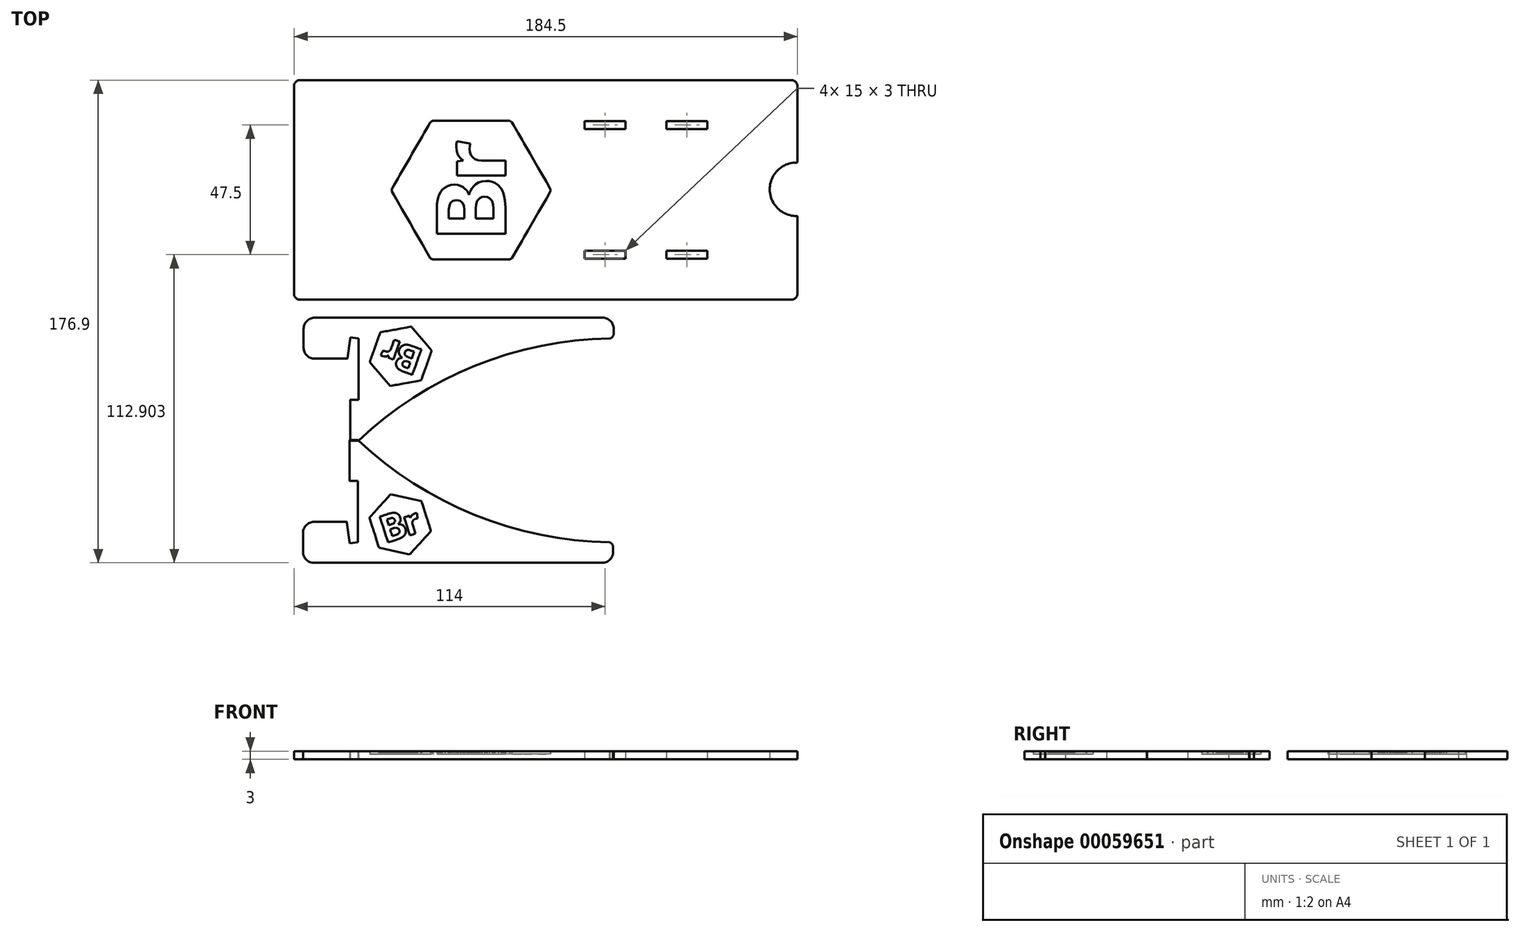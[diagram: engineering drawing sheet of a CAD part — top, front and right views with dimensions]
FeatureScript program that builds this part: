
annotation { "Feature Type Name" : "Feature", "Feature Type Description" : "" }
export const myFeature = defineFeature(function(context is Context, id is Id, definition is map)
    precondition{}
    {
        {
            var Q0;
            Q0=qCreatedBy(makeId("Top.planeOp"),FACE);
            var sketch = newSketch(context, id + "F0", { "sketchPlane" : qUnion([Q0])});
            skLineSegment(sketch, "E0", {"start": v(-68.83, -88.45) * mm, "end": v(20.7, -88.45) * mm});
            skArc(sketch, "E1", {"start": v(20.7, -88.45) * mm, "mid": v(23.52, -87.28) * mm, "end": v(24.7, -84.45) * mm});
            skLineSegment(sketch, "E2", {"start": v(24.7, -84.45) * mm, "end": v(24.7, -82.65) * mm});
            skArc(sketch, "E3", {"start": v(24.7, -82.65) * mm, "mid": v(24.69, -82.75) * mm, "end": v(24.68, -82.85) * mm});
            skLineSegment(sketch, "E4", {"start": v(24.68, -82.85) * mm, "end": v(24.7, -82.63) * mm});
            skArc(sketch, "E5", {"start": v(24.7, -82.63) * mm, "mid": v(24.29, -81.5) * mm, "end": v(23.26, -80.88) * mm});
            skArc(sketch, "E6", {"start": v(23.26, -80.88) * mm, "mid": v(-26.29, -70.78) * mm, "end": v(-68.83, -43.45) * mm});
            skLineSegment(sketch, "E7", {"start": v(-68.83, -43.45) * mm, "end": v(-71.63, -43.45) * mm});
            skArc(sketch, "E8", {"start": v(-71.63, -43.45) * mm, "mid": v(-71.77, -43.51) * mm, "end": v(-71.83, -43.65) * mm});
            skLineSegment(sketch, "E9", {"start": v(-71.83, -43.65) * mm, "end": v(-71.83, -58.25) * mm});
            skArc(sketch, "E10", {"start": v(-71.83, -58.25) * mm, "mid": v(-71.77, -58.4) * mm, "end": v(-71.63, -58.45) * mm});
            skLineSegment(sketch, "E11", {"start": v(-71.63, -58.45) * mm, "end": v(-68.83, -58.45) * mm});
            skLineSegment(sketch, "E12", {"start": v(-68.83, -58.45) * mm, "end": v(-68.83, -73.45) * mm});
            skLineSegment(sketch, "E13", {"start": v(-68.83, -73.45) * mm, "end": v(-68.83, -80.9) * mm});
            skLineSegment(sketch, "E14", {"start": v(-68.83, -80.9) * mm, "end": v(-71.8, -81.3) * mm});
            skLineSegment(sketch, "E15", {"start": v(-71.8, -81.3) * mm, "end": v(-71.86, -80.9) * mm});
            skLineSegment(sketch, "E16", {"start": v(-71.86, -80.9) * mm, "end": v(-72.83, -73.63) * mm});
            skArc(sketch, "E17", {"start": v(-72.83, -73.63) * mm, "mid": v(-72.9, -73.5) * mm, "end": v(-73.03, -73.45) * mm});
            skLineSegment(sketch, "E18", {"start": v(-73.03, -73.45) * mm, "end": v(-84.9, -73.45) * mm});
            skArc(sketch, "E19", {"start": v(-84.9, -73.45) * mm, "mid": v(-87.74, -74.62) * mm, "end": v(-88.9, -77.45) * mm});
            skLineSegment(sketch, "E20", {"start": v(-88.9, -77.45) * mm, "end": v(-88.9, -84.45) * mm});
            skArc(sketch, "E21", {"start": v(-88.9, -84.45) * mm, "mid": v(-87.74, -87.28) * mm, "end": v(-84.9, -88.45) * mm});
            skLineSegment(sketch, "E22", {"start": v(-84.9, -88.45) * mm, "end": v(-71.83, -88.45) * mm});
            skLineSegment(sketch, "E23", {"start": v(-71.83, -88.45) * mm, "end": v(-68.83, -88.45) * mm});
            skLineSegment(sketch, "E24", {"start": v(-68.83, -88.45) * mm, "end": v(-68.83, -88.45) * mm});
            skLineSegment(sketch, "E25", {"start": v(-68.63, 1.35) * mm, "end": v(20.9, 1.35) * mm});
            skArc(sketch, "E26", {"start": v(20.9, 1.35) * mm, "mid": v(23.72, 0.18) * mm, "end": v(24.9, -2.65) * mm});
            skLineSegment(sketch, "E27", {"start": v(24.9, -2.65) * mm, "end": v(24.9, -4.45) * mm});
            skArc(sketch, "E28", {"start": v(24.9, -4.45) * mm, "mid": v(24.89, -4.36) * mm, "end": v(24.88, -4.26) * mm});
            skLineSegment(sketch, "E29", {"start": v(24.88, -4.26) * mm, "end": v(24.9, -4.47) * mm});
            skArc(sketch, "E30", {"start": v(24.9, -4.47) * mm, "mid": v(24.49, -5.6) * mm, "end": v(23.46, -6.22) * mm});
            skArc(sketch, "E31", {"start": v(23.46, -6.22) * mm, "mid": v(-26.09, -16.32) * mm, "end": v(-68.63, -43.65) * mm});
            skLineSegment(sketch, "E32", {"start": v(-68.63, -43.65) * mm, "end": v(-71.43, -43.65) * mm});
            skArc(sketch, "E33", {"start": v(-71.43, -43.65) * mm, "mid": v(-71.57, -43.6) * mm, "end": v(-71.63, -43.45) * mm});
            skLineSegment(sketch, "E34", {"start": v(-71.63, -43.45) * mm, "end": v(-71.63, -28.85) * mm});
            skArc(sketch, "E35", {"start": v(-71.63, -28.85) * mm, "mid": v(-71.57, -28.71) * mm, "end": v(-71.43, -28.65) * mm});
            skLineSegment(sketch, "E36", {"start": v(-71.43, -28.65) * mm, "end": v(-68.63, -28.65) * mm});
            skLineSegment(sketch, "E37", {"start": v(-68.63, -28.65) * mm, "end": v(-68.63, -13.65) * mm});
            skLineSegment(sketch, "E38", {"start": v(-68.63, -13.65) * mm, "end": v(-68.63, -6.2) * mm});
            skLineSegment(sketch, "E39", {"start": v(-68.63, -6.2) * mm, "end": v(-71.6, -5.8) * mm});
            skLineSegment(sketch, "E40", {"start": v(-71.6, -5.8) * mm, "end": v(-71.66, -6.2) * mm});
            skLineSegment(sketch, "E41", {"start": v(-71.66, -6.2) * mm, "end": v(-72.63, -13.48) * mm});
            skArc(sketch, "E42", {"start": v(-72.63, -13.48) * mm, "mid": v(-72.7, -13.6) * mm, "end": v(-72.83, -13.65) * mm});
            skLineSegment(sketch, "E43", {"start": v(-72.83, -13.65) * mm, "end": v(-84.7, -13.65) * mm});
            skArc(sketch, "E44", {"start": v(-84.7, -13.65) * mm, "mid": v(-87.54, -12.48) * mm, "end": v(-88.7, -9.65) * mm});
            skLineSegment(sketch, "E45", {"start": v(-88.7, -9.65) * mm, "end": v(-88.7, -2.65) * mm});
            skArc(sketch, "E46", {"start": v(-88.7, -2.65) * mm, "mid": v(-87.54, 0.18) * mm, "end": v(-84.7, 1.35) * mm});
            skLineSegment(sketch, "E47", {"start": v(-84.7, 1.35) * mm, "end": v(-71.63, 1.35) * mm});
            skLineSegment(sketch, "E48", {"start": v(-71.63, 1.35) * mm, "end": v(-68.63, 1.35) * mm});
            skLineSegment(sketch, "E49", {"start": v(-68.63, 1.35) * mm, "end": v(-68.63, 1.35) * mm});
            skLineSegment(sketch, "E50", {"start": v(92, 58.23) * mm, "end": v(92, 58.23) * mm});
            skLineSegment(sketch, "E51", {"start": v(92, 58.23) * mm, "end": v(91.87, 58.23) * mm});
            skArc(sketch, "E52", {"start": v(91.87, 58.23) * mm, "mid": v(83.37, 53.32) * mm, "end": v(83.37, 43.52) * mm});
            skArc(sketch, "E53", {"start": v(83.37, 43.52) * mm, "mid": v(87.02, 39.9) * mm, "end": v(92, 38.61) * mm});
            skArc(sketch, "E54", {"start": v(92, 38.61) * mm, "mid": v(92.18, 38.54) * mm, "end": v(92.25, 38.36) * mm});
            skLineSegment(sketch, "E55", {"start": v(92.25, 38.36) * mm, "end": v(92.25, 10.2) * mm});
            skArc(sketch, "E56", {"start": v(92.25, 10.2) * mm, "mid": v(91.6, 8.61) * mm, "end": v(90, 7.95) * mm});
            skLineSegment(sketch, "E57", {"start": v(90, 7.95) * mm, "end": v(-28, 7.95) * mm});
            skLineSegment(sketch, "E58", {"start": v(-28, 7.95) * mm, "end": v(-90, 7.95) * mm});
            skArc(sketch, "E59", {"start": v(-90, 7.95) * mm, "mid": v(-91.6, 8.61) * mm, "end": v(-92.25, 10.2) * mm});
            skLineSegment(sketch, "E60", {"start": v(-92.25, 10.2) * mm, "end": v(-92.25, 86.2) * mm});
            skArc(sketch, "E61", {"start": v(-92.25, 86.2) * mm, "mid": v(-91.6, 87.8) * mm, "end": v(-90, 88.45) * mm});
            skLineSegment(sketch, "E62", {"start": v(-90, 88.45) * mm, "end": v(-28, 88.45) * mm});
            skLineSegment(sketch, "E63", {"start": v(-28, 88.45) * mm, "end": v(90, 88.45) * mm});
            skArc(sketch, "E64", {"start": v(90, 88.45) * mm, "mid": v(91.6, 87.8) * mm, "end": v(92.25, 86.2) * mm});
            skLineSegment(sketch, "E65", {"start": v(92.25, 86.2) * mm, "end": v(92.25, 86.05) * mm});
            skLineSegment(sketch, "E66", {"start": v(92.25, 86.05) * mm, "end": v(92.25, 58.48) * mm});
            skArc(sketch, "E67", {"start": v(92.25, 58.48) * mm, "mid": v(92.18, 58.3) * mm, "end": v(92, 58.23) * mm});
            skLineSegment(sketch, "E68", {"start": v(-42.29, 72.97) * mm, "end": v(-43.03, 71.69) * mm});
            skLineSegment(sketch, "E69", {"start": v(-43.03, 71.69) * mm, "end": v(-43.77, 70.4) * mm});
            skLineSegment(sketch, "E70", {"start": v(-43.77, 70.4) * mm, "end": v(-44.5, 69.12) * mm});
            skLineSegment(sketch, "E71", {"start": v(-44.5, 69.12) * mm, "end": v(-45.25, 67.83) * mm});
            skLineSegment(sketch, "E72", {"start": v(-45.25, 67.83) * mm, "end": v(-46, 66.55) * mm});
            skLineSegment(sketch, "E73", {"start": v(-46, 66.55) * mm, "end": v(-46.73, 65.26) * mm});
            skLineSegment(sketch, "E74", {"start": v(-46.73, 65.26) * mm, "end": v(-47.48, 63.98) * mm});
            skLineSegment(sketch, "E75", {"start": v(-47.48, 63.98) * mm, "end": v(-48.22, 62.7) * mm});
            skLineSegment(sketch, "E76", {"start": v(-48.22, 62.7) * mm, "end": v(-48.96, 61.41) * mm});
            skLineSegment(sketch, "E77", {"start": v(-48.96, 61.41) * mm, "end": v(-49.7, 60.13) * mm});
            skLineSegment(sketch, "E78", {"start": v(-49.7, 60.13) * mm, "end": v(-50.44, 58.84) * mm});
            skLineSegment(sketch, "E79", {"start": v(-50.44, 58.84) * mm, "end": v(-51.18, 57.56) * mm});
            skLineSegment(sketch, "E80", {"start": v(-51.18, 57.56) * mm, "end": v(-51.92, 56.27) * mm});
            skLineSegment(sketch, "E81", {"start": v(-51.92, 56.27) * mm, "end": v(-52.67, 55) * mm});
            skLineSegment(sketch, "E82", {"start": v(-52.67, 55) * mm, "end": v(-53.4, 53.7) * mm});
            skLineSegment(sketch, "E83", {"start": v(-53.4, 53.7) * mm, "end": v(-54.15, 52.42) * mm});
            skLineSegment(sketch, "E84", {"start": v(-54.15, 52.42) * mm, "end": v(-54.9, 51.14) * mm});
            skLineSegment(sketch, "E85", {"start": v(-54.9, 51.14) * mm, "end": v(-55.63, 49.85) * mm});
            skLineSegment(sketch, "E86", {"start": v(-55.63, 49.85) * mm, "end": v(-56.37, 48.57) * mm});
            skLineSegment(sketch, "E87", {"start": v(-56.37, 48.57) * mm, "end": v(-56.37, 47.58) * mm});
            skLineSegment(sketch, "E88", {"start": v(-56.37, 47.58) * mm, "end": v(-55.63, 46.3) * mm});
            skLineSegment(sketch, "E89", {"start": v(-55.63, 46.3) * mm, "end": v(-54.9, 45) * mm});
            skLineSegment(sketch, "E90", {"start": v(-54.9, 45) * mm, "end": v(-54.15, 43.72) * mm});
            skLineSegment(sketch, "E91", {"start": v(-54.15, 43.72) * mm, "end": v(-53.4, 42.44) * mm});
            skLineSegment(sketch, "E92", {"start": v(-53.4, 42.44) * mm, "end": v(-52.67, 41.15) * mm});
            skLineSegment(sketch, "E93", {"start": v(-52.67, 41.15) * mm, "end": v(-51.92, 39.87) * mm});
            skLineSegment(sketch, "E94", {"start": v(-51.92, 39.87) * mm, "end": v(-51.18, 38.59) * mm});
            skLineSegment(sketch, "E95", {"start": v(-51.18, 38.59) * mm, "end": v(-50.44, 37.3) * mm});
            skLineSegment(sketch, "E96", {"start": v(-50.44, 37.3) * mm, "end": v(-49.7, 36.02) * mm});
            skLineSegment(sketch, "E97", {"start": v(-49.7, 36.02) * mm, "end": v(-48.96, 34.73) * mm});
            skLineSegment(sketch, "E98", {"start": v(-48.96, 34.73) * mm, "end": v(-48.22, 33.45) * mm});
            skLineSegment(sketch, "E99", {"start": v(-48.22, 33.45) * mm, "end": v(-47.48, 32.16) * mm});
            skLineSegment(sketch, "E100", {"start": v(-47.48, 32.16) * mm, "end": v(-46.73, 30.88) * mm});
            skLineSegment(sketch, "E101", {"start": v(-46.73, 30.88) * mm, "end": v(-46, 29.6) * mm});
            skLineSegment(sketch, "E102", {"start": v(-46, 29.6) * mm, "end": v(-45.25, 28.3) * mm});
            skLineSegment(sketch, "E103", {"start": v(-45.25, 28.3) * mm, "end": v(-44.5, 27.02) * mm});
            skLineSegment(sketch, "E104", {"start": v(-44.5, 27.02) * mm, "end": v(-43.77, 25.74) * mm});
            skLineSegment(sketch, "E105", {"start": v(-43.77, 25.74) * mm, "end": v(-43.03, 24.45) * mm});
            skLineSegment(sketch, "E106", {"start": v(-43.03, 24.45) * mm, "end": v(-42.29, 23.17) * mm});
            skLineSegment(sketch, "E107", {"start": v(-42.29, 23.17) * mm, "end": v(-41.42, 22.67) * mm});
            skLineSegment(sketch, "E108", {"start": v(-41.42, 22.67) * mm, "end": v(-39.94, 22.67) * mm});
            skLineSegment(sketch, "E109", {"start": v(-39.94, 22.67) * mm, "end": v(-38.46, 22.67) * mm});
            skLineSegment(sketch, "E110", {"start": v(-38.46, 22.67) * mm, "end": v(-36.97, 22.67) * mm});
            skLineSegment(sketch, "E111", {"start": v(-36.97, 22.67) * mm, "end": v(-35.49, 22.67) * mm});
            skLineSegment(sketch, "E112", {"start": v(-35.49, 22.67) * mm, "end": v(-34, 22.67) * mm});
            skLineSegment(sketch, "E113", {"start": v(-34, 22.67) * mm, "end": v(-32.52, 22.67) * mm});
            skLineSegment(sketch, "E114", {"start": v(-32.52, 22.67) * mm, "end": v(-31.04, 22.67) * mm});
            skLineSegment(sketch, "E115", {"start": v(-31.04, 22.67) * mm, "end": v(-29.56, 22.67) * mm});
            skLineSegment(sketch, "E116", {"start": v(-29.56, 22.67) * mm, "end": v(-28.07, 22.67) * mm});
            skLineSegment(sketch, "E117", {"start": v(-28.07, 22.67) * mm, "end": v(-26.6, 22.67) * mm});
            skLineSegment(sketch, "E118", {"start": v(-26.6, 22.67) * mm, "end": v(-25.1, 22.67) * mm});
            skLineSegment(sketch, "E119", {"start": v(-25.1, 22.67) * mm, "end": v(-23.63, 22.67) * mm});
            skLineSegment(sketch, "E120", {"start": v(-23.63, 22.67) * mm, "end": v(-22.14, 22.67) * mm});
            skLineSegment(sketch, "E121", {"start": v(-22.14, 22.67) * mm, "end": v(-20.66, 22.67) * mm});
            skLineSegment(sketch, "E122", {"start": v(-20.66, 22.67) * mm, "end": v(-19.18, 22.67) * mm});
            skLineSegment(sketch, "E123", {"start": v(-19.18, 22.67) * mm, "end": v(-17.7, 22.67) * mm});
            skLineSegment(sketch, "E124", {"start": v(-17.7, 22.67) * mm, "end": v(-16.21, 22.67) * mm});
            skLineSegment(sketch, "E125", {"start": v(-16.21, 22.67) * mm, "end": v(-14.73, 22.67) * mm});
            skLineSegment(sketch, "E126", {"start": v(-14.73, 22.67) * mm, "end": v(-13.24, 22.67) * mm});
            skLineSegment(sketch, "E127", {"start": v(-13.24, 22.67) * mm, "end": v(-12.38, 23.17) * mm});
            skLineSegment(sketch, "E128", {"start": v(-12.38, 23.17) * mm, "end": v(-11.64, 24.45) * mm});
            skLineSegment(sketch, "E129", {"start": v(-11.64, 24.45) * mm, "end": v(-10.9, 25.74) * mm});
            skLineSegment(sketch, "E130", {"start": v(-10.9, 25.74) * mm, "end": v(-10.16, 27.02) * mm});
            skLineSegment(sketch, "E131", {"start": v(-10.16, 27.02) * mm, "end": v(-9.42, 28.3) * mm});
            skLineSegment(sketch, "E132", {"start": v(-9.42, 28.3) * mm, "end": v(-8.67, 29.6) * mm});
            skLineSegment(sketch, "E133", {"start": v(-8.67, 29.6) * mm, "end": v(-7.93, 30.87) * mm});
            skLineSegment(sketch, "E134", {"start": v(-7.93, 30.87) * mm, "end": v(-7.2, 32.16) * mm});
            skLineSegment(sketch, "E135", {"start": v(-7.2, 32.16) * mm, "end": v(-6.45, 33.44) * mm});
            skLineSegment(sketch, "E136", {"start": v(-6.45, 33.44) * mm, "end": v(-5.7, 34.73) * mm});
            skLineSegment(sketch, "E137", {"start": v(-5.7, 34.73) * mm, "end": v(-4.97, 36.01) * mm});
            skLineSegment(sketch, "E138", {"start": v(-4.97, 36.01) * mm, "end": v(-4.22, 37.3) * mm});
            skLineSegment(sketch, "E139", {"start": v(-4.22, 37.3) * mm, "end": v(-3.48, 38.58) * mm});
            skLineSegment(sketch, "E140", {"start": v(-3.48, 38.58) * mm, "end": v(-2.74, 39.86) * mm});
            skLineSegment(sketch, "E141", {"start": v(-2.74, 39.86) * mm, "end": v(-2, 41.15) * mm});
            skLineSegment(sketch, "E142", {"start": v(-2, 41.15) * mm, "end": v(-1.26, 42.43) * mm});
            skLineSegment(sketch, "E143", {"start": v(-1.26, 42.43) * mm, "end": v(-0.52, 43.72) * mm});
            skLineSegment(sketch, "E144", {"start": v(-0.52, 43.72) * mm, "end": v(0.22, 45) * mm});
            skLineSegment(sketch, "E145", {"start": v(0.22, 45) * mm, "end": v(0.97, 46.29) * mm});
            skLineSegment(sketch, "E146", {"start": v(0.97, 46.29) * mm, "end": v(1.7, 47.57) * mm});
            skLineSegment(sketch, "E147", {"start": v(1.7, 47.57) * mm, "end": v(1.84, 48.07) * mm});
            skLineSegment(sketch, "E148", {"start": v(1.84, 48.07) * mm, "end": v(1.7, 48.57) * mm});
            skLineSegment(sketch, "E149", {"start": v(1.7, 48.57) * mm, "end": v(0.97, 49.85) * mm});
            skLineSegment(sketch, "E150", {"start": v(0.97, 49.85) * mm, "end": v(0.22, 51.14) * mm});
            skLineSegment(sketch, "E151", {"start": v(0.22, 51.14) * mm, "end": v(-0.52, 52.42) * mm});
            skLineSegment(sketch, "E152", {"start": v(-0.52, 52.42) * mm, "end": v(-1.26, 53.7) * mm});
            skLineSegment(sketch, "E153", {"start": v(-1.26, 53.7) * mm, "end": v(-2, 55) * mm});
            skLineSegment(sketch, "E154", {"start": v(-2, 55) * mm, "end": v(-2.74, 56.28) * mm});
            skLineSegment(sketch, "E155", {"start": v(-2.74, 56.28) * mm, "end": v(-3.48, 57.56) * mm});
            skLineSegment(sketch, "E156", {"start": v(-3.48, 57.56) * mm, "end": v(-4.22, 58.85) * mm});
            skLineSegment(sketch, "E157", {"start": v(-4.22, 58.85) * mm, "end": v(-4.97, 60.13) * mm});
            skLineSegment(sketch, "E158", {"start": v(-4.97, 60.13) * mm, "end": v(-5.7, 61.42) * mm});
            skLineSegment(sketch, "E159", {"start": v(-5.7, 61.42) * mm, "end": v(-6.45, 62.7) * mm});
            skLineSegment(sketch, "E160", {"start": v(-6.45, 62.7) * mm, "end": v(-7.2, 63.99) * mm});
            skLineSegment(sketch, "E161", {"start": v(-7.2, 63.99) * mm, "end": v(-7.93, 65.27) * mm});
            skLineSegment(sketch, "E162", {"start": v(-7.93, 65.27) * mm, "end": v(-8.67, 66.55) * mm});
            skLineSegment(sketch, "E163", {"start": v(-8.67, 66.55) * mm, "end": v(-9.42, 67.84) * mm});
            skLineSegment(sketch, "E164", {"start": v(-9.42, 67.84) * mm, "end": v(-10.16, 69.12) * mm});
            skLineSegment(sketch, "E165", {"start": v(-10.16, 69.12) * mm, "end": v(-10.9, 70.4) * mm});
            skLineSegment(sketch, "E166", {"start": v(-10.9, 70.4) * mm, "end": v(-11.64, 71.7) * mm});
            skLineSegment(sketch, "E167", {"start": v(-11.64, 71.7) * mm, "end": v(-12.38, 72.98) * mm});
            skLineSegment(sketch, "E168", {"start": v(-12.38, 72.98) * mm, "end": v(-13.24, 73.48) * mm});
            skLineSegment(sketch, "E169", {"start": v(-13.24, 73.48) * mm, "end": v(-14.73, 73.48) * mm});
            skLineSegment(sketch, "E170", {"start": v(-14.73, 73.48) * mm, "end": v(-16.21, 73.48) * mm});
            skLineSegment(sketch, "E171", {"start": v(-16.21, 73.48) * mm, "end": v(-17.7, 73.48) * mm});
            skLineSegment(sketch, "E172", {"start": v(-17.7, 73.48) * mm, "end": v(-19.18, 73.48) * mm});
            skLineSegment(sketch, "E173", {"start": v(-19.18, 73.48) * mm, "end": v(-20.66, 73.48) * mm});
            skLineSegment(sketch, "E174", {"start": v(-20.66, 73.48) * mm, "end": v(-22.14, 73.48) * mm});
            skLineSegment(sketch, "E175", {"start": v(-22.14, 73.48) * mm, "end": v(-23.63, 73.48) * mm});
            skLineSegment(sketch, "E176", {"start": v(-23.63, 73.48) * mm, "end": v(-25.1, 73.48) * mm});
            skLineSegment(sketch, "E177", {"start": v(-25.1, 73.48) * mm, "end": v(-26.6, 73.48) * mm});
            skLineSegment(sketch, "E178", {"start": v(-26.6, 73.48) * mm, "end": v(-28.07, 73.48) * mm});
            skLineSegment(sketch, "E179", {"start": v(-28.07, 73.48) * mm, "end": v(-29.56, 73.48) * mm});
            skLineSegment(sketch, "E180", {"start": v(-29.56, 73.48) * mm, "end": v(-31.04, 73.48) * mm});
            skLineSegment(sketch, "E181", {"start": v(-31.04, 73.48) * mm, "end": v(-32.52, 73.48) * mm});
            skLineSegment(sketch, "E182", {"start": v(-32.52, 73.48) * mm, "end": v(-34, 73.48) * mm});
            skLineSegment(sketch, "E183", {"start": v(-34, 73.48) * mm, "end": v(-35.49, 73.48) * mm});
            skLineSegment(sketch, "E184", {"start": v(-35.49, 73.48) * mm, "end": v(-36.97, 73.48) * mm});
            skLineSegment(sketch, "E185", {"start": v(-36.97, 73.48) * mm, "end": v(-38.46, 73.48) * mm});
            skLineSegment(sketch, "E186", {"start": v(-38.46, 73.48) * mm, "end": v(-39.94, 73.48) * mm});
            skLineSegment(sketch, "E187", {"start": v(-39.94, 73.48) * mm, "end": v(-41.42, 73.48) * mm});
            skLineSegment(sketch, "E188", {"start": v(-41.42, 73.48) * mm, "end": v(-42.29, 72.97) * mm});
            skLineSegment(sketch, "E189", {"start": v(-29.84, 41.08) * mm, "end": v(-30, 42.34) * mm});
            skLineSegment(sketch, "E190", {"start": v(-30, 42.34) * mm, "end": v(-30.47, 43.43) * mm});
            skLineSegment(sketch, "E191", {"start": v(-30.47, 43.43) * mm, "end": v(-31.33, 44.2) * mm});
            skLineSegment(sketch, "E192", {"start": v(-31.33, 44.2) * mm, "end": v(-32.67, 44.5) * mm});
            skLineSegment(sketch, "E193", {"start": v(-32.67, 44.5) * mm, "end": v(-34.04, 44.2) * mm});
            skLineSegment(sketch, "E194", {"start": v(-34.04, 44.2) * mm, "end": v(-34.9, 43.41) * mm});
            skLineSegment(sketch, "E195", {"start": v(-34.9, 43.41) * mm, "end": v(-35.35, 42.3) * mm});
            skLineSegment(sketch, "E196", {"start": v(-35.35, 42.3) * mm, "end": v(-35.49, 41.08) * mm});
            skLineSegment(sketch, "E197", {"start": v(-35.49, 41.08) * mm, "end": v(-35.49, 39.96) * mm});
            skLineSegment(sketch, "E198", {"start": v(-35.49, 39.96) * mm, "end": v(-35.49, 38.84) * mm});
            skLineSegment(sketch, "E199", {"start": v(-35.49, 38.84) * mm, "end": v(-35.49, 37.72) * mm});
            skLineSegment(sketch, "E200", {"start": v(-35.49, 37.72) * mm, "end": v(-34.07, 37.72) * mm});
            skLineSegment(sketch, "E201", {"start": v(-34.07, 37.72) * mm, "end": v(-32.66, 37.72) * mm});
            skLineSegment(sketch, "E202", {"start": v(-32.66, 37.72) * mm, "end": v(-31.24, 37.72) * mm});
            skLineSegment(sketch, "E203", {"start": v(-31.24, 37.72) * mm, "end": v(-29.83, 37.72) * mm});
            skLineSegment(sketch, "E204", {"start": v(-29.83, 37.72) * mm, "end": v(-29.83, 38.84) * mm});
            skLineSegment(sketch, "E205", {"start": v(-29.83, 38.84) * mm, "end": v(-29.83, 39.96) * mm});
            skLineSegment(sketch, "E206", {"start": v(-29.83, 39.96) * mm, "end": v(-29.83, 41.08) * mm});
            skLineSegment(sketch, "E207", {"start": v(-29.83, 41.08) * mm, "end": v(-29.84, 41.08) * mm});
            skLineSegment(sketch, "E208", {"start": v(-32.44, 53.51) * mm, "end": v(-32.44, 54.81) * mm});
            skLineSegment(sketch, "E209", {"start": v(-32.44, 54.81) * mm, "end": v(-32.44, 56.11) * mm});
            skLineSegment(sketch, "E210", {"start": v(-32.44, 56.11) * mm, "end": v(-32.44, 57.41) * mm});
            skLineSegment(sketch, "E211", {"start": v(-32.44, 57.41) * mm, "end": v(-32.44, 58.71) * mm});
            skLineSegment(sketch, "E212", {"start": v(-32.44, 58.71) * mm, "end": v(-31.33, 58.8) * mm});
            skLineSegment(sketch, "E213", {"start": v(-31.33, 58.8) * mm, "end": v(-30.21, 58.9) * mm});
            skLineSegment(sketch, "E214", {"start": v(-30.21, 58.9) * mm, "end": v(-31.1, 59.7) * mm});
            skLineSegment(sketch, "E215", {"start": v(-31.1, 59.7) * mm, "end": v(-31.95, 60.76) * mm});
            skLineSegment(sketch, "E216", {"start": v(-31.95, 60.76) * mm, "end": v(-32.4, 61.63) * mm});
            skLineSegment(sketch, "E217", {"start": v(-32.4, 61.63) * mm, "end": v(-32.68, 62.65) * mm});
            skLineSegment(sketch, "E218", {"start": v(-32.68, 62.65) * mm, "end": v(-32.78, 63.83) * mm});
            skLineSegment(sketch, "E219", {"start": v(-32.78, 63.83) * mm, "end": v(-32.7, 65.06) * mm});
            skLineSegment(sketch, "E220", {"start": v(-32.7, 65.06) * mm, "end": v(-32.44, 66.06) * mm});
            skLineSegment(sketch, "E221", {"start": v(-32.44, 66.06) * mm, "end": v(-31.24, 65.84) * mm});
            skLineSegment(sketch, "E222", {"start": v(-31.24, 65.84) * mm, "end": v(-30.05, 65.63) * mm});
            skLineSegment(sketch, "E223", {"start": v(-30.05, 65.63) * mm, "end": v(-28.85, 65.41) * mm});
            skLineSegment(sketch, "E224", {"start": v(-28.85, 65.41) * mm, "end": v(-27.66, 65.2) * mm});
            skLineSegment(sketch, "E225", {"start": v(-27.66, 65.2) * mm, "end": v(-27.85, 64.3) * mm});
            skLineSegment(sketch, "E226", {"start": v(-27.85, 64.3) * mm, "end": v(-27.92, 63.24) * mm});
            skLineSegment(sketch, "E227", {"start": v(-27.92, 63.24) * mm, "end": v(-27.8, 62.04) * mm});
            skLineSegment(sketch, "E228", {"start": v(-27.8, 62.04) * mm, "end": v(-27.4, 61) * mm});
            skLineSegment(sketch, "E229", {"start": v(-27.4, 61) * mm, "end": v(-26.77, 60.13) * mm});
            skLineSegment(sketch, "E230", {"start": v(-26.77, 60.13) * mm, "end": v(-25.9, 59.48) * mm});
            skLineSegment(sketch, "E231", {"start": v(-25.9, 59.48) * mm, "end": v(-24.8, 59.08) * mm});
            skLineSegment(sketch, "E232", {"start": v(-24.8, 59.08) * mm, "end": v(-23.5, 58.95) * mm});
            skLineSegment(sketch, "E233", {"start": v(-23.5, 58.95) * mm, "end": v(-22.05, 58.95) * mm});
            skLineSegment(sketch, "E234", {"start": v(-22.05, 58.95) * mm, "end": v(-20.6, 58.95) * mm});
            skLineSegment(sketch, "E235", {"start": v(-20.6, 58.95) * mm, "end": v(-19.13, 58.95) * mm});
            skLineSegment(sketch, "E236", {"start": v(-19.13, 58.95) * mm, "end": v(-17.68, 58.95) * mm});
            skLineSegment(sketch, "E237", {"start": v(-17.68, 58.95) * mm, "end": v(-16.22, 58.95) * mm});
            skLineSegment(sketch, "E238", {"start": v(-16.22, 58.95) * mm, "end": v(-14.76, 58.95) * mm});
            skLineSegment(sketch, "E239", {"start": v(-14.76, 58.95) * mm, "end": v(-14.76, 57.6) * mm});
            skLineSegment(sketch, "E240", {"start": v(-14.76, 57.6) * mm, "end": v(-14.76, 56.24) * mm});
            skLineSegment(sketch, "E241", {"start": v(-14.76, 56.24) * mm, "end": v(-14.76, 54.88) * mm});
            skLineSegment(sketch, "E242", {"start": v(-14.76, 54.88) * mm, "end": v(-14.76, 53.52) * mm});
            skLineSegment(sketch, "E243", {"start": v(-14.76, 53.52) * mm, "end": v(-16.23, 53.52) * mm});
            skLineSegment(sketch, "E244", {"start": v(-16.23, 53.52) * mm, "end": v(-17.7, 53.52) * mm});
            skLineSegment(sketch, "E245", {"start": v(-17.7, 53.52) * mm, "end": v(-19.18, 53.52) * mm});
            skLineSegment(sketch, "E246", {"start": v(-19.18, 53.52) * mm, "end": v(-20.65, 53.52) * mm});
            skLineSegment(sketch, "E247", {"start": v(-20.65, 53.52) * mm, "end": v(-22.13, 53.52) * mm});
            skLineSegment(sketch, "E248", {"start": v(-22.13, 53.52) * mm, "end": v(-23.6, 53.52) * mm});
            skLineSegment(sketch, "E249", {"start": v(-23.6, 53.52) * mm, "end": v(-25.07, 53.52) * mm});
            skLineSegment(sketch, "E250", {"start": v(-25.07, 53.52) * mm, "end": v(-26.55, 53.52) * mm});
            skLineSegment(sketch, "E251", {"start": v(-26.55, 53.52) * mm, "end": v(-28.02, 53.52) * mm});
            skLineSegment(sketch, "E252", {"start": v(-28.02, 53.52) * mm, "end": v(-29.5, 53.52) * mm});
            skLineSegment(sketch, "E253", {"start": v(-29.5, 53.52) * mm, "end": v(-30.97, 53.52) * mm});
            skLineSegment(sketch, "E254", {"start": v(-30.97, 53.52) * mm, "end": v(-32.44, 53.52) * mm});
            skLineSegment(sketch, "E255", {"start": v(-32.44, 53.52) * mm, "end": v(-32.44, 53.51) * mm});
            skLineSegment(sketch, "E256", {"start": v(-39.9, 32.19) * mm, "end": v(-39.9, 33.53) * mm});
            skLineSegment(sketch, "E257", {"start": v(-39.9, 33.53) * mm, "end": v(-39.9, 34.88) * mm});
            skLineSegment(sketch, "E258", {"start": v(-39.9, 34.88) * mm, "end": v(-39.9, 36.22) * mm});
            skLineSegment(sketch, "E259", {"start": v(-39.9, 36.22) * mm, "end": v(-39.9, 37.57) * mm});
            skLineSegment(sketch, "E260", {"start": v(-39.9, 37.57) * mm, "end": v(-39.9, 38.92) * mm});
            skLineSegment(sketch, "E261", {"start": v(-39.9, 38.92) * mm, "end": v(-39.9, 40.26) * mm});
            skLineSegment(sketch, "E262", {"start": v(-39.9, 40.26) * mm, "end": v(-39.9, 41.6) * mm});
            skLineSegment(sketch, "E263", {"start": v(-39.9, 41.6) * mm, "end": v(-39.84, 43.09) * mm});
            skLineSegment(sketch, "E264", {"start": v(-39.84, 43.09) * mm, "end": v(-39.66, 44.4) * mm});
            skLineSegment(sketch, "E265", {"start": v(-39.66, 44.4) * mm, "end": v(-39.36, 45.56) * mm});
            skLineSegment(sketch, "E266", {"start": v(-39.36, 45.56) * mm, "end": v(-38.95, 46.58) * mm});
            skLineSegment(sketch, "E267", {"start": v(-38.95, 46.58) * mm, "end": v(-38.47, 47.46) * mm});
            skLineSegment(sketch, "E268", {"start": v(-38.47, 47.46) * mm, "end": v(-37.9, 48.2) * mm});
            skLineSegment(sketch, "E269", {"start": v(-37.9, 48.2) * mm, "end": v(-36.93, 49.08) * mm});
            skLineSegment(sketch, "E270", {"start": v(-36.93, 49.08) * mm, "end": v(-35.82, 49.68) * mm});
            skLineSegment(sketch, "E271", {"start": v(-35.82, 49.68) * mm, "end": v(-34.6, 50.02) * mm});
            skLineSegment(sketch, "E272", {"start": v(-34.6, 50.02) * mm, "end": v(-33.34, 50.13) * mm});
            skLineSegment(sketch, "E273", {"start": v(-33.34, 50.13) * mm, "end": v(-32.2, 50.02) * mm});
            skLineSegment(sketch, "E274", {"start": v(-32.2, 50.02) * mm, "end": v(-31.22, 49.7) * mm});
            skLineSegment(sketch, "E275", {"start": v(-31.22, 49.7) * mm, "end": v(-30.36, 49.22) * mm});
            skLineSegment(sketch, "E276", {"start": v(-30.36, 49.22) * mm, "end": v(-29.64, 48.68) * mm});
            skLineSegment(sketch, "E277", {"start": v(-29.64, 48.68) * mm, "end": v(-29.05, 48.08) * mm});
            skLineSegment(sketch, "E278", {"start": v(-29.05, 48.08) * mm, "end": v(-28.6, 47.43) * mm});
            skLineSegment(sketch, "E279", {"start": v(-28.6, 47.43) * mm, "end": v(-28.11, 46.36) * mm});
            skLineSegment(sketch, "E280", {"start": v(-28.11, 46.36) * mm, "end": v(-27.88, 47.06) * mm});
            skLineSegment(sketch, "E281", {"start": v(-27.88, 47.06) * mm, "end": v(-27.55, 47.87) * mm});
            skLineSegment(sketch, "E282", {"start": v(-27.55, 47.87) * mm, "end": v(-27.08, 48.74) * mm});
            skLineSegment(sketch, "E283", {"start": v(-27.08, 48.74) * mm, "end": v(-26.44, 49.56) * mm});
            skLineSegment(sketch, "E284", {"start": v(-26.44, 49.56) * mm, "end": v(-25.6, 50.29) * mm});
            skLineSegment(sketch, "E285", {"start": v(-25.6, 50.29) * mm, "end": v(-24.6, 50.9) * mm});
            skLineSegment(sketch, "E286", {"start": v(-24.6, 50.9) * mm, "end": v(-23.38, 51.3) * mm});
            skLineSegment(sketch, "E287", {"start": v(-23.38, 51.3) * mm, "end": v(-21.97, 51.45) * mm});
            skLineSegment(sketch, "E288", {"start": v(-21.97, 51.45) * mm, "end": v(-20.74, 51.37) * mm});
            skLineSegment(sketch, "E289", {"start": v(-20.74, 51.37) * mm, "end": v(-19.63, 51.14) * mm});
            skLineSegment(sketch, "E290", {"start": v(-19.63, 51.14) * mm, "end": v(-18.66, 50.75) * mm});
            skLineSegment(sketch, "E291", {"start": v(-18.66, 50.75) * mm, "end": v(-17.42, 49.91) * mm});
            skLineSegment(sketch, "E292", {"start": v(-17.42, 49.91) * mm, "end": v(-16.43, 48.8) * mm});
            skLineSegment(sketch, "E293", {"start": v(-16.43, 48.8) * mm, "end": v(-15.9, 47.9) * mm});
            skLineSegment(sketch, "E294", {"start": v(-15.9, 47.9) * mm, "end": v(-15.48, 46.86) * mm});
            skLineSegment(sketch, "E295", {"start": v(-15.48, 46.86) * mm, "end": v(-15.17, 45.7) * mm});
            skLineSegment(sketch, "E296", {"start": v(-15.17, 45.7) * mm, "end": v(-14.95, 44.44) * mm});
            skLineSegment(sketch, "E297", {"start": v(-14.95, 44.44) * mm, "end": v(-14.81, 43.08) * mm});
            skLineSegment(sketch, "E298", {"start": v(-14.81, 43.08) * mm, "end": v(-14.77, 41.62) * mm});
            skLineSegment(sketch, "E299", {"start": v(-14.77, 41.62) * mm, "end": v(-14.77, 40.27) * mm});
            skLineSegment(sketch, "E300", {"start": v(-14.77, 40.27) * mm, "end": v(-14.77, 38.92) * mm});
            skLineSegment(sketch, "E301", {"start": v(-14.77, 38.92) * mm, "end": v(-14.77, 37.58) * mm});
            skLineSegment(sketch, "E302", {"start": v(-14.77, 37.58) * mm, "end": v(-14.77, 36.23) * mm});
            skLineSegment(sketch, "E303", {"start": v(-14.77, 36.23) * mm, "end": v(-14.77, 34.88) * mm});
            skLineSegment(sketch, "E304", {"start": v(-14.77, 34.88) * mm, "end": v(-14.77, 33.53) * mm});
            skLineSegment(sketch, "E305", {"start": v(-14.77, 33.53) * mm, "end": v(-14.77, 32.19) * mm});
            skLineSegment(sketch, "E306", {"start": v(-14.77, 32.19) * mm, "end": v(-16.25, 32.19) * mm});
            skLineSegment(sketch, "E307", {"start": v(-16.25, 32.19) * mm, "end": v(-17.73, 32.19) * mm});
            skLineSegment(sketch, "E308", {"start": v(-17.73, 32.19) * mm, "end": v(-19.2, 32.19) * mm});
            skLineSegment(sketch, "E309", {"start": v(-19.2, 32.19) * mm, "end": v(-20.68, 32.19) * mm});
            skLineSegment(sketch, "E310", {"start": v(-20.68, 32.19) * mm, "end": v(-22.16, 32.19) * mm});
            skLineSegment(sketch, "E311", {"start": v(-22.16, 32.19) * mm, "end": v(-23.64, 32.19) * mm});
            skLineSegment(sketch, "E312", {"start": v(-23.64, 32.19) * mm, "end": v(-25.12, 32.19) * mm});
            skLineSegment(sketch, "E313", {"start": v(-25.12, 32.19) * mm, "end": v(-26.6, 32.19) * mm});
            skLineSegment(sketch, "E314", {"start": v(-26.6, 32.19) * mm, "end": v(-28.08, 32.19) * mm});
            skLineSegment(sketch, "E315", {"start": v(-28.08, 32.19) * mm, "end": v(-29.56, 32.19) * mm});
            skLineSegment(sketch, "E316", {"start": v(-29.56, 32.19) * mm, "end": v(-31.03, 32.19) * mm});
            skLineSegment(sketch, "E317", {"start": v(-31.03, 32.19) * mm, "end": v(-32.51, 32.19) * mm});
            skLineSegment(sketch, "E318", {"start": v(-32.51, 32.19) * mm, "end": v(-34, 32.19) * mm});
            skLineSegment(sketch, "E319", {"start": v(-34, 32.19) * mm, "end": v(-35.47, 32.19) * mm});
            skLineSegment(sketch, "E320", {"start": v(-35.47, 32.19) * mm, "end": v(-36.95, 32.19) * mm});
            skLineSegment(sketch, "E321", {"start": v(-36.95, 32.19) * mm, "end": v(-38.43, 32.19) * mm});
            skLineSegment(sketch, "E322", {"start": v(-38.43, 32.19) * mm, "end": v(-39.9, 32.19) * mm});
            skLineSegment(sketch, "E323", {"start": v(-19.14, 41.41) * mm, "end": v(-19.23, 42.77) * mm});
            skLineSegment(sketch, "E324", {"start": v(-19.23, 42.77) * mm, "end": v(-19.66, 44.17) * mm});
            skLineSegment(sketch, "E325", {"start": v(-19.66, 44.17) * mm, "end": v(-20.64, 45.24) * mm});
            skLineSegment(sketch, "E326", {"start": v(-20.64, 45.24) * mm, "end": v(-21.4, 45.57) * mm});
            skLineSegment(sketch, "E327", {"start": v(-21.4, 45.57) * mm, "end": v(-22.41, 45.67) * mm});
            skLineSegment(sketch, "E328", {"start": v(-22.41, 45.67) * mm, "end": v(-23.34, 45.57) * mm});
            skLineSegment(sketch, "E329", {"start": v(-23.34, 45.57) * mm, "end": v(-24.07, 45.26) * mm});
            skLineSegment(sketch, "E330", {"start": v(-24.07, 45.26) * mm, "end": v(-25.07, 44.2) * mm});
            skLineSegment(sketch, "E331", {"start": v(-25.07, 44.2) * mm, "end": v(-25.56, 42.8) * mm});
            skLineSegment(sketch, "E332", {"start": v(-25.56, 42.8) * mm, "end": v(-25.7, 41.4) * mm});
            skLineSegment(sketch, "E333", {"start": v(-25.7, 41.4) * mm, "end": v(-25.7, 40.18) * mm});
            skLineSegment(sketch, "E334", {"start": v(-25.7, 40.18) * mm, "end": v(-25.7, 38.94) * mm});
            skLineSegment(sketch, "E335", {"start": v(-25.7, 38.94) * mm, "end": v(-25.7, 37.71) * mm});
            skLineSegment(sketch, "E336", {"start": v(-25.7, 37.71) * mm, "end": v(-24.39, 37.71) * mm});
            skLineSegment(sketch, "E337", {"start": v(-24.39, 37.71) * mm, "end": v(-23.07, 37.71) * mm});
            skLineSegment(sketch, "E338", {"start": v(-23.07, 37.71) * mm, "end": v(-21.76, 37.71) * mm});
            skLineSegment(sketch, "E339", {"start": v(-21.76, 37.71) * mm, "end": v(-20.45, 37.71) * mm});
            skLineSegment(sketch, "E340", {"start": v(-20.45, 37.71) * mm, "end": v(-19.14, 37.71) * mm});
            skLineSegment(sketch, "E341", {"start": v(-19.14, 37.71) * mm, "end": v(-19.14, 38.95) * mm});
            skLineSegment(sketch, "E342", {"start": v(-19.14, 38.95) * mm, "end": v(-19.14, 40.18) * mm});
            skLineSegment(sketch, "E343", {"start": v(-19.14, 40.18) * mm, "end": v(-19.14, 41.41) * mm});
            skLineSegment(sketch, "E344", {"start": v(-64.33, -15.03) * mm, "end": v(-63.95, -15.47) * mm});
            skLineSegment(sketch, "E345", {"start": v(-63.95, -15.47) * mm, "end": v(-63.57, -15.92) * mm});
            skLineSegment(sketch, "E346", {"start": v(-63.57, -15.92) * mm, "end": v(-63.2, -16.36) * mm});
            skLineSegment(sketch, "E347", {"start": v(-63.2, -16.36) * mm, "end": v(-62.81, -16.8) * mm});
            skLineSegment(sketch, "E348", {"start": v(-62.81, -16.8) * mm, "end": v(-62.44, -17.25) * mm});
            skLineSegment(sketch, "E349", {"start": v(-62.44, -17.25) * mm, "end": v(-62.06, -17.7) * mm});
            skLineSegment(sketch, "E350", {"start": v(-62.06, -17.7) * mm, "end": v(-61.68, -18.14) * mm});
            skLineSegment(sketch, "E351", {"start": v(-61.68, -18.14) * mm, "end": v(-61.3, -18.58) * mm});
            skLineSegment(sketch, "E352", {"start": v(-61.3, -18.58) * mm, "end": v(-60.92, -19.03) * mm});
            skLineSegment(sketch, "E353", {"start": v(-60.92, -19.03) * mm, "end": v(-60.54, -19.47) * mm});
            skLineSegment(sketch, "E354", {"start": v(-60.54, -19.47) * mm, "end": v(-60.17, -19.92) * mm});
            skLineSegment(sketch, "E355", {"start": v(-60.17, -19.92) * mm, "end": v(-59.79, -20.36) * mm});
            skLineSegment(sketch, "E356", {"start": v(-59.79, -20.36) * mm, "end": v(-59.4, -20.8) * mm});
            skLineSegment(sketch, "E357", {"start": v(-59.4, -20.8) * mm, "end": v(-59.03, -21.25) * mm});
            skLineSegment(sketch, "E358", {"start": v(-59.03, -21.25) * mm, "end": v(-58.65, -21.7) * mm});
            skLineSegment(sketch, "E359", {"start": v(-58.65, -21.7) * mm, "end": v(-58.27, -22.14) * mm});
            skLineSegment(sketch, "E360", {"start": v(-58.27, -22.14) * mm, "end": v(-57.9, -22.59) * mm});
            skLineSegment(sketch, "E361", {"start": v(-57.9, -22.59) * mm, "end": v(-57.52, -23.03) * mm});
            skLineSegment(sketch, "E362", {"start": v(-57.52, -23.03) * mm, "end": v(-57.14, -23.47) * mm});
            skLineSegment(sketch, "E363", {"start": v(-57.14, -23.47) * mm, "end": v(-56.77, -23.6) * mm});
            skLineSegment(sketch, "E364", {"start": v(-56.77, -23.6) * mm, "end": v(-56.2, -23.5) * mm});
            skLineSegment(sketch, "E365", {"start": v(-56.2, -23.5) * mm, "end": v(-55.62, -23.4) * mm});
            skLineSegment(sketch, "E366", {"start": v(-55.62, -23.4) * mm, "end": v(-55.05, -23.29) * mm});
            skLineSegment(sketch, "E367", {"start": v(-55.05, -23.29) * mm, "end": v(-54.47, -23.18) * mm});
            skLineSegment(sketch, "E368", {"start": v(-54.47, -23.18) * mm, "end": v(-53.9, -23.08) * mm});
            skLineSegment(sketch, "E369", {"start": v(-53.9, -23.08) * mm, "end": v(-53.33, -22.97) * mm});
            skLineSegment(sketch, "E370", {"start": v(-53.33, -22.97) * mm, "end": v(-52.75, -22.87) * mm});
            skLineSegment(sketch, "E371", {"start": v(-52.75, -22.87) * mm, "end": v(-52.18, -22.76) * mm});
            skLineSegment(sketch, "E372", {"start": v(-52.18, -22.76) * mm, "end": v(-51.6, -22.66) * mm});
            skLineSegment(sketch, "E373", {"start": v(-51.6, -22.66) * mm, "end": v(-51.03, -22.55) * mm});
            skLineSegment(sketch, "E374", {"start": v(-51.03, -22.55) * mm, "end": v(-50.45, -22.45) * mm});
            skLineSegment(sketch, "E375", {"start": v(-50.45, -22.45) * mm, "end": v(-49.88, -22.34) * mm});
            skLineSegment(sketch, "E376", {"start": v(-49.88, -22.34) * mm, "end": v(-49.3, -22.24) * mm});
            skLineSegment(sketch, "E377", {"start": v(-49.3, -22.24) * mm, "end": v(-48.73, -22.13) * mm});
            skLineSegment(sketch, "E378", {"start": v(-48.73, -22.13) * mm, "end": v(-48.16, -22.03) * mm});
            skLineSegment(sketch, "E379", {"start": v(-48.16, -22.03) * mm, "end": v(-47.58, -21.92) * mm});
            skLineSegment(sketch, "E380", {"start": v(-47.58, -21.92) * mm, "end": v(-47, -21.82) * mm});
            skLineSegment(sketch, "E381", {"start": v(-47, -21.82) * mm, "end": v(-46.43, -21.7) * mm});
            skLineSegment(sketch, "E382", {"start": v(-46.43, -21.7) * mm, "end": v(-45.86, -21.6) * mm});
            skLineSegment(sketch, "E383", {"start": v(-45.86, -21.6) * mm, "end": v(-45.56, -21.35) * mm});
            skLineSegment(sketch, "E384", {"start": v(-45.56, -21.35) * mm, "end": v(-45.36, -20.8) * mm});
            skLineSegment(sketch, "E385", {"start": v(-45.36, -20.8) * mm, "end": v(-45.17, -20.25) * mm});
            skLineSegment(sketch, "E386", {"start": v(-45.17, -20.25) * mm, "end": v(-44.97, -19.7) * mm});
            skLineSegment(sketch, "E387", {"start": v(-44.97, -19.7) * mm, "end": v(-44.78, -19.15) * mm});
            skLineSegment(sketch, "E388", {"start": v(-44.78, -19.15) * mm, "end": v(-44.58, -18.6) * mm});
            skLineSegment(sketch, "E389", {"start": v(-44.58, -18.6) * mm, "end": v(-44.38, -18.05) * mm});
            skLineSegment(sketch, "E390", {"start": v(-44.38, -18.05) * mm, "end": v(-44.19, -17.5) * mm});
            skLineSegment(sketch, "E391", {"start": v(-44.19, -17.5) * mm, "end": v(-44, -16.95) * mm});
            skLineSegment(sketch, "E392", {"start": v(-44, -16.95) * mm, "end": v(-43.8, -16.4) * mm});
            skLineSegment(sketch, "E393", {"start": v(-43.8, -16.4) * mm, "end": v(-43.6, -15.85) * mm});
            skLineSegment(sketch, "E394", {"start": v(-43.6, -15.85) * mm, "end": v(-43.4, -15.3) * mm});
            skLineSegment(sketch, "E395", {"start": v(-43.4, -15.3) * mm, "end": v(-43.2, -14.75) * mm});
            skLineSegment(sketch, "E396", {"start": v(-43.2, -14.75) * mm, "end": v(-43.01, -14.2) * mm});
            skLineSegment(sketch, "E397", {"start": v(-43.01, -14.2) * mm, "end": v(-42.82, -13.65) * mm});
            skLineSegment(sketch, "E398", {"start": v(-42.82, -13.65) * mm, "end": v(-42.62, -13.1) * mm});
            skLineSegment(sketch, "E399", {"start": v(-42.62, -13.1) * mm, "end": v(-42.43, -12.55) * mm});
            skLineSegment(sketch, "E400", {"start": v(-42.43, -12.55) * mm, "end": v(-42.23, -12) * mm});
            skLineSegment(sketch, "E401", {"start": v(-42.23, -12) * mm, "end": v(-42.03, -11.45) * mm});
            skLineSegment(sketch, "E402", {"start": v(-42.03, -11.45) * mm, "end": v(-41.84, -10.9) * mm});
            skLineSegment(sketch, "E403", {"start": v(-41.84, -10.9) * mm, "end": v(-41.9, -10.51) * mm});
            skLineSegment(sketch, "E404", {"start": v(-41.9, -10.51) * mm, "end": v(-42.29, -10.07) * mm});
            skLineSegment(sketch, "E405", {"start": v(-42.29, -10.07) * mm, "end": v(-42.67, -9.63) * mm});
            skLineSegment(sketch, "E406", {"start": v(-42.67, -9.63) * mm, "end": v(-43.04, -9.18) * mm});
            skLineSegment(sketch, "E407", {"start": v(-43.04, -9.18) * mm, "end": v(-43.42, -8.74) * mm});
            skLineSegment(sketch, "E408", {"start": v(-43.42, -8.74) * mm, "end": v(-43.8, -8.3) * mm});
            skLineSegment(sketch, "E409", {"start": v(-43.8, -8.3) * mm, "end": v(-44.18, -7.85) * mm});
            skLineSegment(sketch, "E410", {"start": v(-44.18, -7.85) * mm, "end": v(-44.56, -7.4) * mm});
            skLineSegment(sketch, "E411", {"start": v(-44.56, -7.4) * mm, "end": v(-44.94, -6.96) * mm});
            skLineSegment(sketch, "E412", {"start": v(-44.94, -6.96) * mm, "end": v(-45.31, -6.51) * mm});
            skLineSegment(sketch, "E413", {"start": v(-45.31, -6.51) * mm, "end": v(-45.7, -6.07) * mm});
            skLineSegment(sketch, "E414", {"start": v(-45.7, -6.07) * mm, "end": v(-46.07, -5.62) * mm});
            skLineSegment(sketch, "E415", {"start": v(-46.07, -5.62) * mm, "end": v(-46.45, -5.18) * mm});
            skLineSegment(sketch, "E416", {"start": v(-46.45, -5.18) * mm, "end": v(-46.83, -4.74) * mm});
            skLineSegment(sketch, "E417", {"start": v(-46.83, -4.74) * mm, "end": v(-47.2, -4.3) * mm});
            skLineSegment(sketch, "E418", {"start": v(-47.2, -4.3) * mm, "end": v(-47.58, -3.85) * mm});
            skLineSegment(sketch, "E419", {"start": v(-47.58, -3.85) * mm, "end": v(-47.96, -3.4) * mm});
            skLineSegment(sketch, "E420", {"start": v(-47.96, -3.4) * mm, "end": v(-48.34, -2.96) * mm});
            skLineSegment(sketch, "E421", {"start": v(-48.34, -2.96) * mm, "end": v(-48.72, -2.51) * mm});
            skLineSegment(sketch, "E422", {"start": v(-48.72, -2.51) * mm, "end": v(-49.1, -2.07) * mm});
            skLineSegment(sketch, "E423", {"start": v(-49.1, -2.07) * mm, "end": v(-49.26, -1.95) * mm});
            skLineSegment(sketch, "E424", {"start": v(-49.26, -1.95) * mm, "end": v(-49.47, -1.94) * mm});
            skLineSegment(sketch, "E425", {"start": v(-49.47, -1.94) * mm, "end": v(-50.04, -2.04) * mm});
            skLineSegment(sketch, "E426", {"start": v(-50.04, -2.04) * mm, "end": v(-50.62, -2.15) * mm});
            skLineSegment(sketch, "E427", {"start": v(-50.62, -2.15) * mm, "end": v(-51.2, -2.25) * mm});
            skLineSegment(sketch, "E428", {"start": v(-51.2, -2.25) * mm, "end": v(-51.77, -2.36) * mm});
            skLineSegment(sketch, "E429", {"start": v(-51.77, -2.36) * mm, "end": v(-52.34, -2.46) * mm});
            skLineSegment(sketch, "E430", {"start": v(-52.34, -2.46) * mm, "end": v(-52.91, -2.57) * mm});
            skLineSegment(sketch, "E431", {"start": v(-52.91, -2.57) * mm, "end": v(-53.49, -2.67) * mm});
            skLineSegment(sketch, "E432", {"start": v(-53.49, -2.67) * mm, "end": v(-54.06, -2.78) * mm});
            skLineSegment(sketch, "E433", {"start": v(-54.06, -2.78) * mm, "end": v(-54.64, -2.88) * mm});
            skLineSegment(sketch, "E434", {"start": v(-54.64, -2.88) * mm, "end": v(-55.21, -2.99) * mm});
            skLineSegment(sketch, "E435", {"start": v(-55.21, -2.99) * mm, "end": v(-55.79, -3.1) * mm});
            skLineSegment(sketch, "E436", {"start": v(-55.79, -3.1) * mm, "end": v(-56.36, -3.2) * mm});
            skLineSegment(sketch, "E437", {"start": v(-56.36, -3.2) * mm, "end": v(-56.93, -3.3) * mm});
            skLineSegment(sketch, "E438", {"start": v(-56.93, -3.3) * mm, "end": v(-57.5, -3.41) * mm});
            skLineSegment(sketch, "E439", {"start": v(-57.5, -3.41) * mm, "end": v(-58.08, -3.52) * mm});
            skLineSegment(sketch, "E440", {"start": v(-58.08, -3.52) * mm, "end": v(-58.66, -3.62) * mm});
            skLineSegment(sketch, "E441", {"start": v(-58.66, -3.62) * mm, "end": v(-59.23, -3.73) * mm});
            skLineSegment(sketch, "E442", {"start": v(-59.23, -3.73) * mm, "end": v(-59.8, -3.83) * mm});
            skLineSegment(sketch, "E443", {"start": v(-59.8, -3.83) * mm, "end": v(-60.38, -3.94) * mm});
            skLineSegment(sketch, "E444", {"start": v(-60.38, -3.94) * mm, "end": v(-60.68, -4.2) * mm});
            skLineSegment(sketch, "E445", {"start": v(-60.68, -4.2) * mm, "end": v(-60.88, -4.74) * mm});
            skLineSegment(sketch, "E446", {"start": v(-60.88, -4.74) * mm, "end": v(-61.07, -5.3) * mm});
            skLineSegment(sketch, "E447", {"start": v(-61.07, -5.3) * mm, "end": v(-61.27, -5.84) * mm});
            skLineSegment(sketch, "E448", {"start": v(-61.27, -5.84) * mm, "end": v(-61.46, -6.4) * mm});
            skLineSegment(sketch, "E449", {"start": v(-61.46, -6.4) * mm, "end": v(-61.66, -6.94) * mm});
            skLineSegment(sketch, "E450", {"start": v(-61.66, -6.94) * mm, "end": v(-61.86, -7.5) * mm});
            skLineSegment(sketch, "E451", {"start": v(-61.86, -7.5) * mm, "end": v(-62.05, -8.04) * mm});
            skLineSegment(sketch, "E452", {"start": v(-62.05, -8.04) * mm, "end": v(-62.25, -8.6) * mm});
            skLineSegment(sketch, "E453", {"start": v(-62.25, -8.6) * mm, "end": v(-62.44, -9.14) * mm});
            skLineSegment(sketch, "E454", {"start": v(-62.44, -9.14) * mm, "end": v(-62.64, -9.7) * mm});
            skLineSegment(sketch, "E455", {"start": v(-62.64, -9.7) * mm, "end": v(-62.83, -10.24) * mm});
            skLineSegment(sketch, "E456", {"start": v(-62.83, -10.24) * mm, "end": v(-63.03, -10.8) * mm});
            skLineSegment(sketch, "E457", {"start": v(-63.03, -10.8) * mm, "end": v(-63.23, -11.34) * mm});
            skLineSegment(sketch, "E458", {"start": v(-63.23, -11.34) * mm, "end": v(-63.42, -11.9) * mm});
            skLineSegment(sketch, "E459", {"start": v(-63.42, -11.9) * mm, "end": v(-63.62, -12.44) * mm});
            skLineSegment(sketch, "E460", {"start": v(-63.62, -12.44) * mm, "end": v(-63.81, -13) * mm});
            skLineSegment(sketch, "E461", {"start": v(-63.81, -13) * mm, "end": v(-64, -13.54) * mm});
            skLineSegment(sketch, "E462", {"start": v(-64, -13.54) * mm, "end": v(-64.2, -14.1) * mm});
            skLineSegment(sketch, "E463", {"start": v(-64.2, -14.1) * mm, "end": v(-64.4, -14.64) * mm});
            skLineSegment(sketch, "E464", {"start": v(-64.4, -14.64) * mm, "end": v(-64.33, -15.03) * mm});
            skLineSegment(sketch, "E465", {"start": v(-55.81, -13.95) * mm, "end": v(-56.3, -13.77) * mm});
            skLineSegment(sketch, "E466", {"start": v(-56.3, -13.77) * mm, "end": v(-56.78, -13.6) * mm});
            skLineSegment(sketch, "E467", {"start": v(-56.78, -13.6) * mm, "end": v(-57.26, -13.43) * mm});
            skLineSegment(sketch, "E468", {"start": v(-57.26, -13.43) * mm, "end": v(-57.74, -13.26) * mm});
            skLineSegment(sketch, "E469", {"start": v(-57.74, -13.26) * mm, "end": v(-57.63, -12.83) * mm});
            skLineSegment(sketch, "E470", {"start": v(-57.63, -12.83) * mm, "end": v(-57.51, -12.4) * mm});
            skLineSegment(sketch, "E471", {"start": v(-57.51, -12.4) * mm, "end": v(-57.93, -12.63) * mm});
            skLineSegment(sketch, "E472", {"start": v(-57.93, -12.63) * mm, "end": v(-58.43, -12.8) * mm});
            skLineSegment(sketch, "E473", {"start": v(-58.43, -12.8) * mm, "end": v(-58.82, -12.86) * mm});
            skLineSegment(sketch, "E474", {"start": v(-58.82, -12.86) * mm, "end": v(-59.23, -12.83) * mm});
            skLineSegment(sketch, "E475", {"start": v(-59.23, -12.83) * mm, "end": v(-59.68, -12.7) * mm});
            skLineSegment(sketch, "E476", {"start": v(-59.68, -12.7) * mm, "end": v(-60.13, -12.52) * mm});
            skLineSegment(sketch, "E477", {"start": v(-60.13, -12.52) * mm, "end": v(-60.46, -12.29) * mm});
            skLineSegment(sketch, "E478", {"start": v(-60.46, -12.29) * mm, "end": v(-60.23, -11.87) * mm});
            skLineSegment(sketch, "E479", {"start": v(-60.23, -11.87) * mm, "end": v(-59.99, -11.46) * mm});
            skLineSegment(sketch, "E480", {"start": v(-59.99, -11.46) * mm, "end": v(-59.75, -11.04) * mm});
            skLineSegment(sketch, "E481", {"start": v(-59.75, -11.04) * mm, "end": v(-59.51, -10.63) * mm});
            skLineSegment(sketch, "E482", {"start": v(-59.51, -10.63) * mm, "end": v(-59.2, -10.82) * mm});
            skLineSegment(sketch, "E483", {"start": v(-59.2, -10.82) * mm, "end": v(-58.82, -10.98) * mm});
            skLineSegment(sketch, "E484", {"start": v(-58.82, -10.98) * mm, "end": v(-58.36, -11.1) * mm});
            skLineSegment(sketch, "E485", {"start": v(-58.36, -11.1) * mm, "end": v(-57.93, -11.1) * mm});
            skLineSegment(sketch, "E486", {"start": v(-57.93, -11.1) * mm, "end": v(-57.52, -10.97) * mm});
            skLineSegment(sketch, "E487", {"start": v(-57.52, -10.97) * mm, "end": v(-57.16, -10.73) * mm});
            skLineSegment(sketch, "E488", {"start": v(-57.16, -10.73) * mm, "end": v(-56.87, -10.38) * mm});
            skLineSegment(sketch, "E489", {"start": v(-56.87, -10.38) * mm, "end": v(-56.65, -9.92) * mm});
            skLineSegment(sketch, "E490", {"start": v(-56.65, -9.92) * mm, "end": v(-56.45, -9.37) * mm});
            skLineSegment(sketch, "E491", {"start": v(-56.45, -9.37) * mm, "end": v(-56.26, -8.83) * mm});
            skLineSegment(sketch, "E492", {"start": v(-56.26, -8.83) * mm, "end": v(-56.07, -8.3) * mm});
            skLineSegment(sketch, "E493", {"start": v(-56.07, -8.3) * mm, "end": v(-55.88, -7.75) * mm});
            skLineSegment(sketch, "E494", {"start": v(-55.88, -7.75) * mm, "end": v(-55.68, -7.21) * mm});
            skLineSegment(sketch, "E495", {"start": v(-55.68, -7.21) * mm, "end": v(-55.5, -6.67) * mm});
            skLineSegment(sketch, "E496", {"start": v(-55.5, -6.67) * mm, "end": v(-54.99, -6.85) * mm});
            skLineSegment(sketch, "E497", {"start": v(-54.99, -6.85) * mm, "end": v(-54.49, -7.03) * mm});
            skLineSegment(sketch, "E498", {"start": v(-54.49, -7.03) * mm, "end": v(-53.98, -7.2) * mm});
            skLineSegment(sketch, "E499", {"start": v(-53.98, -7.2) * mm, "end": v(-53.48, -7.39) * mm});
            skLineSegment(sketch, "E500", {"start": v(-53.48, -7.39) * mm, "end": v(-53.67, -7.93) * mm});
            skLineSegment(sketch, "E501", {"start": v(-53.67, -7.93) * mm, "end": v(-53.87, -8.48) * mm});
            skLineSegment(sketch, "E502", {"start": v(-53.87, -8.48) * mm, "end": v(-54.06, -9.03) * mm});
            skLineSegment(sketch, "E503", {"start": v(-54.06, -9.03) * mm, "end": v(-54.26, -9.57) * mm});
            skLineSegment(sketch, "E504", {"start": v(-54.26, -9.57) * mm, "end": v(-54.45, -10.12) * mm});
            skLineSegment(sketch, "E505", {"start": v(-54.45, -10.12) * mm, "end": v(-54.65, -10.67) * mm});
            skLineSegment(sketch, "E506", {"start": v(-54.65, -10.67) * mm, "end": v(-54.84, -11.21) * mm});
            skLineSegment(sketch, "E507", {"start": v(-54.84, -11.21) * mm, "end": v(-55.04, -11.76) * mm});
            skLineSegment(sketch, "E508", {"start": v(-55.04, -11.76) * mm, "end": v(-55.23, -12.3) * mm});
            skLineSegment(sketch, "E509", {"start": v(-55.23, -12.3) * mm, "end": v(-55.43, -12.85) * mm});
            skLineSegment(sketch, "E510", {"start": v(-55.43, -12.85) * mm, "end": v(-55.62, -13.4) * mm});
            skLineSegment(sketch, "E511", {"start": v(-55.62, -13.4) * mm, "end": v(-55.81, -13.94) * mm});
            skLineSegment(sketch, "E512", {"start": v(-55.81, -13.94) * mm, "end": v(-55.81, -13.95) * mm});
            skLineSegment(sketch, "E513", {"start": v(-48.89, -19.53) * mm, "end": v(-49.39, -19.35) * mm});
            skLineSegment(sketch, "E514", {"start": v(-49.39, -19.35) * mm, "end": v(-49.89, -19.18) * mm});
            skLineSegment(sketch, "E515", {"start": v(-49.89, -19.18) * mm, "end": v(-50.39, -19) * mm});
            skLineSegment(sketch, "E516", {"start": v(-50.39, -19) * mm, "end": v(-50.89, -18.82) * mm});
            skLineSegment(sketch, "E517", {"start": v(-50.89, -18.82) * mm, "end": v(-51.38, -18.64) * mm});
            skLineSegment(sketch, "E518", {"start": v(-51.38, -18.64) * mm, "end": v(-51.88, -18.46) * mm});
            skLineSegment(sketch, "E519", {"start": v(-51.88, -18.46) * mm, "end": v(-52.38, -18.29) * mm});
            skLineSegment(sketch, "E520", {"start": v(-52.38, -18.29) * mm, "end": v(-52.92, -18.07) * mm});
            skLineSegment(sketch, "E521", {"start": v(-52.92, -18.07) * mm, "end": v(-53.39, -17.83) * mm});
            skLineSegment(sketch, "E522", {"start": v(-53.39, -17.83) * mm, "end": v(-53.78, -17.56) * mm});
            skLineSegment(sketch, "E523", {"start": v(-53.78, -17.56) * mm, "end": v(-54.1, -17.28) * mm});
            skLineSegment(sketch, "E524", {"start": v(-54.1, -17.28) * mm, "end": v(-54.36, -16.98) * mm});
            skLineSegment(sketch, "E525", {"start": v(-54.36, -16.98) * mm, "end": v(-54.56, -16.67) * mm});
            skLineSegment(sketch, "E526", {"start": v(-54.56, -16.67) * mm, "end": v(-54.76, -16.2) * mm});
            skLineSegment(sketch, "E527", {"start": v(-54.76, -16.2) * mm, "end": v(-54.84, -15.7) * mm});
            skLineSegment(sketch, "E528", {"start": v(-54.84, -15.7) * mm, "end": v(-54.8, -15.21) * mm});
            skLineSegment(sketch, "E529", {"start": v(-54.8, -15.21) * mm, "end": v(-54.68, -14.73) * mm});
            skLineSegment(sketch, "E530", {"start": v(-54.68, -14.73) * mm, "end": v(-54.49, -14.32) * mm});
            skLineSegment(sketch, "E531", {"start": v(-54.49, -14.32) * mm, "end": v(-54.23, -14) * mm});
            skLineSegment(sketch, "E532", {"start": v(-54.23, -14) * mm, "end": v(-53.95, -13.74) * mm});
            skLineSegment(sketch, "E533", {"start": v(-53.95, -13.74) * mm, "end": v(-53.65, -13.54) * mm});
            skLineSegment(sketch, "E534", {"start": v(-53.65, -13.54) * mm, "end": v(-53.35, -13.4) * mm});
            skLineSegment(sketch, "E535", {"start": v(-53.35, -13.4) * mm, "end": v(-53.05, -13.33) * mm});
            skLineSegment(sketch, "E536", {"start": v(-53.05, -13.33) * mm, "end": v(-52.59, -13.29) * mm});
            skLineSegment(sketch, "E537", {"start": v(-52.59, -13.29) * mm, "end": v(-52.81, -13.1) * mm});
            skLineSegment(sketch, "E538", {"start": v(-52.81, -13.1) * mm, "end": v(-53.07, -12.88) * mm});
            skLineSegment(sketch, "E539", {"start": v(-53.07, -12.88) * mm, "end": v(-53.33, -12.59) * mm});
            skLineSegment(sketch, "E540", {"start": v(-53.33, -12.59) * mm, "end": v(-53.55, -12.24) * mm});
            skLineSegment(sketch, "E541", {"start": v(-53.55, -12.24) * mm, "end": v(-53.71, -11.84) * mm});
            skLineSegment(sketch, "E542", {"start": v(-53.71, -11.84) * mm, "end": v(-53.8, -11.38) * mm});
            skLineSegment(sketch, "E543", {"start": v(-53.8, -11.38) * mm, "end": v(-53.8, -10.88) * mm});
            skLineSegment(sketch, "E544", {"start": v(-53.8, -10.88) * mm, "end": v(-53.66, -10.34) * mm});
            skLineSegment(sketch, "E545", {"start": v(-53.66, -10.34) * mm, "end": v(-53.47, -9.89) * mm});
            skLineSegment(sketch, "E546", {"start": v(-53.47, -9.89) * mm, "end": v(-53.24, -9.5) * mm});
            skLineSegment(sketch, "E547", {"start": v(-53.24, -9.5) * mm, "end": v(-52.97, -9.2) * mm});
            skLineSegment(sketch, "E548", {"start": v(-52.97, -9.2) * mm, "end": v(-52.5, -8.85) * mm});
            skLineSegment(sketch, "E549", {"start": v(-52.5, -8.85) * mm, "end": v(-51.95, -8.63) * mm});
            skLineSegment(sketch, "E550", {"start": v(-51.95, -8.63) * mm, "end": v(-51.54, -8.56) * mm});
            skLineSegment(sketch, "E551", {"start": v(-51.54, -8.56) * mm, "end": v(-51.1, -8.54) * mm});
            skLineSegment(sketch, "E552", {"start": v(-51.1, -8.54) * mm, "end": v(-50.64, -8.57) * mm});
            skLineSegment(sketch, "E553", {"start": v(-50.64, -8.57) * mm, "end": v(-50.14, -8.66) * mm});
            skLineSegment(sketch, "E554", {"start": v(-50.14, -8.66) * mm, "end": v(-49.61, -8.79) * mm});
            skLineSegment(sketch, "E555", {"start": v(-49.61, -8.79) * mm, "end": v(-49.07, -8.96) * mm});
            skLineSegment(sketch, "E556", {"start": v(-49.07, -8.96) * mm, "end": v(-48.57, -9.14) * mm});
            skLineSegment(sketch, "E557", {"start": v(-48.57, -9.14) * mm, "end": v(-48.07, -9.32) * mm});
            skLineSegment(sketch, "E558", {"start": v(-48.07, -9.32) * mm, "end": v(-47.57, -9.5) * mm});
            skLineSegment(sketch, "E559", {"start": v(-47.57, -9.5) * mm, "end": v(-47.07, -9.68) * mm});
            skLineSegment(sketch, "E560", {"start": v(-47.07, -9.68) * mm, "end": v(-46.57, -9.85) * mm});
            skLineSegment(sketch, "E561", {"start": v(-46.57, -9.85) * mm, "end": v(-46.07, -10.03) * mm});
            skLineSegment(sketch, "E562", {"start": v(-46.07, -10.03) * mm, "end": v(-45.57, -10.2) * mm});
            skLineSegment(sketch, "E563", {"start": v(-45.57, -10.2) * mm, "end": v(-45.76, -10.76) * mm});
            skLineSegment(sketch, "E564", {"start": v(-45.76, -10.76) * mm, "end": v(-45.96, -11.3) * mm});
            skLineSegment(sketch, "E565", {"start": v(-45.96, -11.3) * mm, "end": v(-46.15, -11.85) * mm});
            skLineSegment(sketch, "E566", {"start": v(-46.15, -11.85) * mm, "end": v(-46.35, -12.4) * mm});
            skLineSegment(sketch, "E567", {"start": v(-46.35, -12.4) * mm, "end": v(-46.54, -12.95) * mm});
            skLineSegment(sketch, "E568", {"start": v(-46.54, -12.95) * mm, "end": v(-46.74, -13.5) * mm});
            skLineSegment(sketch, "E569", {"start": v(-46.74, -13.5) * mm, "end": v(-46.94, -14.05) * mm});
            skLineSegment(sketch, "E570", {"start": v(-46.94, -14.05) * mm, "end": v(-47.13, -14.6) * mm});
            skLineSegment(sketch, "E571", {"start": v(-47.13, -14.6) * mm, "end": v(-47.33, -15.14) * mm});
            skLineSegment(sketch, "E572", {"start": v(-47.33, -15.14) * mm, "end": v(-47.52, -15.7) * mm});
            skLineSegment(sketch, "E573", {"start": v(-47.52, -15.7) * mm, "end": v(-47.72, -16.24) * mm});
            skLineSegment(sketch, "E574", {"start": v(-47.72, -16.24) * mm, "end": v(-47.91, -16.79) * mm});
            skLineSegment(sketch, "E575", {"start": v(-47.91, -16.79) * mm, "end": v(-48.1, -17.34) * mm});
            skLineSegment(sketch, "E576", {"start": v(-48.1, -17.34) * mm, "end": v(-48.3, -17.89) * mm});
            skLineSegment(sketch, "E577", {"start": v(-48.3, -17.89) * mm, "end": v(-48.5, -18.43) * mm});
            skLineSegment(sketch, "E578", {"start": v(-48.5, -18.43) * mm, "end": v(-48.7, -18.98) * mm});
            skLineSegment(sketch, "E579", {"start": v(-48.7, -18.98) * mm, "end": v(-48.89, -19.53) * mm});
            skLineSegment(sketch, "E580", {"start": v(-49.57, -10.61) * mm, "end": v(-50.08, -10.47) * mm});
            skLineSegment(sketch, "E581", {"start": v(-50.08, -10.47) * mm, "end": v(-50.66, -10.44) * mm});
            skLineSegment(sketch, "E582", {"start": v(-50.66, -10.44) * mm, "end": v(-51.19, -10.66) * mm});
            skLineSegment(sketch, "E583", {"start": v(-51.19, -10.66) * mm, "end": v(-51.4, -10.9) * mm});
            skLineSegment(sketch, "E584", {"start": v(-51.4, -10.9) * mm, "end": v(-51.58, -11.26) * mm});
            skLineSegment(sketch, "E585", {"start": v(-51.58, -11.26) * mm, "end": v(-51.66, -11.62) * mm});
            skLineSegment(sketch, "E586", {"start": v(-51.66, -11.62) * mm, "end": v(-51.65, -11.93) * mm});
            skLineSegment(sketch, "E587", {"start": v(-51.65, -11.93) * mm, "end": v(-51.38, -12.44) * mm});
            skLineSegment(sketch, "E588", {"start": v(-51.38, -12.44) * mm, "end": v(-50.93, -12.81) * mm});
            skLineSegment(sketch, "E589", {"start": v(-50.93, -12.81) * mm, "end": v(-50.43, -13.05) * mm});
            skLineSegment(sketch, "E590", {"start": v(-50.43, -13.05) * mm, "end": v(-49.97, -13.2) * mm});
            skLineSegment(sketch, "E591", {"start": v(-49.97, -13.2) * mm, "end": v(-49.52, -13.37) * mm});
            skLineSegment(sketch, "E592", {"start": v(-49.52, -13.37) * mm, "end": v(-49.06, -13.53) * mm});
            skLineSegment(sketch, "E593", {"start": v(-49.06, -13.53) * mm, "end": v(-48.89, -13.05) * mm});
            skLineSegment(sketch, "E594", {"start": v(-48.89, -13.05) * mm, "end": v(-48.72, -12.56) * mm});
            skLineSegment(sketch, "E595", {"start": v(-48.72, -12.56) * mm, "end": v(-48.54, -12.07) * mm});
            skLineSegment(sketch, "E596", {"start": v(-48.54, -12.07) * mm, "end": v(-48.37, -11.59) * mm});
            skLineSegment(sketch, "E597", {"start": v(-48.37, -11.59) * mm, "end": v(-48.2, -11.1) * mm});
            skLineSegment(sketch, "E598", {"start": v(-48.2, -11.1) * mm, "end": v(-48.65, -10.94) * mm});
            skLineSegment(sketch, "E599", {"start": v(-48.65, -10.94) * mm, "end": v(-49.11, -10.77) * mm});
            skLineSegment(sketch, "E600", {"start": v(-49.11, -10.77) * mm, "end": v(-49.57, -10.61) * mm});
            skLineSegment(sketch, "E601", {"start": v(-50.86, -14.62) * mm, "end": v(-51.34, -14.51) * mm});
            skLineSegment(sketch, "E602", {"start": v(-51.34, -14.51) * mm, "end": v(-51.81, -14.55) * mm});
            skLineSegment(sketch, "E603", {"start": v(-51.81, -14.55) * mm, "end": v(-52.21, -14.76) * mm});
            skLineSegment(sketch, "E604", {"start": v(-52.21, -14.76) * mm, "end": v(-52.5, -15.22) * mm});
            skLineSegment(sketch, "E605", {"start": v(-52.5, -15.22) * mm, "end": v(-52.57, -15.77) * mm});
            skLineSegment(sketch, "E606", {"start": v(-52.57, -15.77) * mm, "end": v(-52.4, -16.2) * mm});
            skLineSegment(sketch, "E607", {"start": v(-52.4, -16.2) * mm, "end": v(-52.04, -16.5) * mm});
            skLineSegment(sketch, "E608", {"start": v(-52.04, -16.5) * mm, "end": v(-51.6, -16.72) * mm});
            skLineSegment(sketch, "E609", {"start": v(-51.6, -16.72) * mm, "end": v(-51.19, -16.87) * mm});
            skLineSegment(sketch, "E610", {"start": v(-51.19, -16.87) * mm, "end": v(-50.77, -17.01) * mm});
            skLineSegment(sketch, "E611", {"start": v(-50.77, -17.01) * mm, "end": v(-50.36, -17.16) * mm});
            skLineSegment(sketch, "E612", {"start": v(-50.36, -17.16) * mm, "end": v(-50.17, -16.64) * mm});
            skLineSegment(sketch, "E613", {"start": v(-50.17, -16.64) * mm, "end": v(-49.98, -16.11) * mm});
            skLineSegment(sketch, "E614", {"start": v(-49.98, -16.11) * mm, "end": v(-49.8, -15.59) * mm});
            skLineSegment(sketch, "E615", {"start": v(-49.8, -15.59) * mm, "end": v(-49.61, -15.06) * mm});
            skLineSegment(sketch, "E616", {"start": v(-49.61, -15.06) * mm, "end": v(-50.03, -14.92) * mm});
            skLineSegment(sketch, "E617", {"start": v(-50.03, -14.92) * mm, "end": v(-50.44, -14.77) * mm});
            skLineSegment(sketch, "E618", {"start": v(-50.44, -14.77) * mm, "end": v(-50.85, -14.62) * mm});
            skLineSegment(sketch, "E619", {"start": v(-50.85, -14.62) * mm, "end": v(-50.86, -14.62) * mm});
            skLineSegment(sketch, "E620", {"start": v(-45.76, -65.75) * mm, "end": v(-46.34, -65.63) * mm});
            skLineSegment(sketch, "E621", {"start": v(-46.34, -65.63) * mm, "end": v(-46.9, -65.5) * mm});
            skLineSegment(sketch, "E622", {"start": v(-46.9, -65.5) * mm, "end": v(-47.48, -65.38) * mm});
            skLineSegment(sketch, "E623", {"start": v(-47.48, -65.38) * mm, "end": v(-48.05, -65.25) * mm});
            skLineSegment(sketch, "E624", {"start": v(-48.05, -65.25) * mm, "end": v(-48.62, -65.13) * mm});
            skLineSegment(sketch, "E625", {"start": v(-48.62, -65.13) * mm, "end": v(-49.19, -65) * mm});
            skLineSegment(sketch, "E626", {"start": v(-49.19, -65) * mm, "end": v(-49.76, -64.88) * mm});
            skLineSegment(sketch, "E627", {"start": v(-49.76, -64.88) * mm, "end": v(-50.33, -64.75) * mm});
            skLineSegment(sketch, "E628", {"start": v(-50.33, -64.75) * mm, "end": v(-50.9, -64.63) * mm});
            skLineSegment(sketch, "E629", {"start": v(-50.9, -64.63) * mm, "end": v(-51.47, -64.5) * mm});
            skLineSegment(sketch, "E630", {"start": v(-51.47, -64.5) * mm, "end": v(-52.04, -64.38) * mm});
            skLineSegment(sketch, "E631", {"start": v(-52.04, -64.38) * mm, "end": v(-52.6, -64.26) * mm});
            skLineSegment(sketch, "E632", {"start": v(-52.6, -64.26) * mm, "end": v(-53.18, -64.13) * mm});
            skLineSegment(sketch, "E633", {"start": v(-53.18, -64.13) * mm, "end": v(-53.75, -64) * mm});
            skLineSegment(sketch, "E634", {"start": v(-53.75, -64) * mm, "end": v(-54.32, -63.88) * mm});
            skLineSegment(sketch, "E635", {"start": v(-54.32, -63.88) * mm, "end": v(-54.89, -63.76) * mm});
            skLineSegment(sketch, "E636", {"start": v(-54.89, -63.76) * mm, "end": v(-55.46, -63.63) * mm});
            skLineSegment(sketch, "E637", {"start": v(-55.46, -63.63) * mm, "end": v(-56.03, -63.5) * mm});
            skLineSegment(sketch, "E638", {"start": v(-56.03, -63.5) * mm, "end": v(-56.6, -63.38) * mm});
            skLineSegment(sketch, "E639", {"start": v(-56.6, -63.38) * mm, "end": v(-56.97, -63.5) * mm});
            skLineSegment(sketch, "E640", {"start": v(-56.97, -63.5) * mm, "end": v(-57.36, -63.93) * mm});
            skLineSegment(sketch, "E641", {"start": v(-57.36, -63.93) * mm, "end": v(-57.76, -64.36) * mm});
            skLineSegment(sketch, "E642", {"start": v(-57.76, -64.36) * mm, "end": v(-58.15, -64.8) * mm});
            skLineSegment(sketch, "E643", {"start": v(-58.15, -64.8) * mm, "end": v(-58.55, -65.23) * mm});
            skLineSegment(sketch, "E644", {"start": v(-58.55, -65.23) * mm, "end": v(-58.94, -65.66) * mm});
            skLineSegment(sketch, "E645", {"start": v(-58.94, -65.66) * mm, "end": v(-59.33, -66.09) * mm});
            skLineSegment(sketch, "E646", {"start": v(-59.33, -66.09) * mm, "end": v(-59.73, -66.52) * mm});
            skLineSegment(sketch, "E647", {"start": v(-59.73, -66.52) * mm, "end": v(-60.12, -66.95) * mm});
            skLineSegment(sketch, "E648", {"start": v(-60.12, -66.95) * mm, "end": v(-60.51, -67.38) * mm});
            skLineSegment(sketch, "E649", {"start": v(-60.51, -67.38) * mm, "end": v(-60.9, -67.81) * mm});
            skLineSegment(sketch, "E650", {"start": v(-60.9, -67.81) * mm, "end": v(-61.3, -68.25) * mm});
            skLineSegment(sketch, "E651", {"start": v(-61.3, -68.25) * mm, "end": v(-61.7, -68.68) * mm});
            skLineSegment(sketch, "E652", {"start": v(-61.7, -68.68) * mm, "end": v(-62.09, -69.1) * mm});
            skLineSegment(sketch, "E653", {"start": v(-62.09, -69.1) * mm, "end": v(-62.48, -69.54) * mm});
            skLineSegment(sketch, "E654", {"start": v(-62.48, -69.54) * mm, "end": v(-62.87, -69.97) * mm});
            skLineSegment(sketch, "E655", {"start": v(-62.87, -69.97) * mm, "end": v(-63.27, -70.4) * mm});
            skLineSegment(sketch, "E656", {"start": v(-63.27, -70.4) * mm, "end": v(-63.66, -70.83) * mm});
            skLineSegment(sketch, "E657", {"start": v(-63.66, -70.83) * mm, "end": v(-64.05, -71.27) * mm});
            skLineSegment(sketch, "E658", {"start": v(-64.05, -71.27) * mm, "end": v(-64.45, -71.7) * mm});
            skLineSegment(sketch, "E659", {"start": v(-64.45, -71.7) * mm, "end": v(-64.53, -72.08) * mm});
            skLineSegment(sketch, "E660", {"start": v(-64.53, -72.08) * mm, "end": v(-64.35, -72.64) * mm});
            skLineSegment(sketch, "E661", {"start": v(-64.35, -72.64) * mm, "end": v(-64.18, -73.2) * mm});
            skLineSegment(sketch, "E662", {"start": v(-64.18, -73.2) * mm, "end": v(-64, -73.75) * mm});
            skLineSegment(sketch, "E663", {"start": v(-64, -73.75) * mm, "end": v(-63.82, -74.3) * mm});
            skLineSegment(sketch, "E664", {"start": v(-63.82, -74.3) * mm, "end": v(-63.65, -74.86) * mm});
            skLineSegment(sketch, "E665", {"start": v(-63.65, -74.86) * mm, "end": v(-63.47, -75.42) * mm});
            skLineSegment(sketch, "E666", {"start": v(-63.47, -75.42) * mm, "end": v(-63.3, -75.98) * mm});
            skLineSegment(sketch, "E667", {"start": v(-63.3, -75.98) * mm, "end": v(-63.12, -76.53) * mm});
            skLineSegment(sketch, "E668", {"start": v(-63.12, -76.53) * mm, "end": v(-62.94, -77.09) * mm});
            skLineSegment(sketch, "E669", {"start": v(-62.94, -77.09) * mm, "end": v(-62.76, -77.64) * mm});
            skLineSegment(sketch, "E670", {"start": v(-62.76, -77.64) * mm, "end": v(-62.58, -78.2) * mm});
            skLineSegment(sketch, "E671", {"start": v(-62.58, -78.2) * mm, "end": v(-62.4, -78.76) * mm});
            skLineSegment(sketch, "E672", {"start": v(-62.4, -78.76) * mm, "end": v(-62.23, -79.31) * mm});
            skLineSegment(sketch, "E673", {"start": v(-62.23, -79.31) * mm, "end": v(-62.05, -79.87) * mm});
            skLineSegment(sketch, "E674", {"start": v(-62.05, -79.87) * mm, "end": v(-61.88, -80.43) * mm});
            skLineSegment(sketch, "E675", {"start": v(-61.88, -80.43) * mm, "end": v(-61.7, -80.98) * mm});
            skLineSegment(sketch, "E676", {"start": v(-61.7, -80.98) * mm, "end": v(-61.52, -81.54) * mm});
            skLineSegment(sketch, "E677", {"start": v(-61.52, -81.54) * mm, "end": v(-61.35, -82.1) * mm});
            skLineSegment(sketch, "E678", {"start": v(-61.35, -82.1) * mm, "end": v(-61.17, -82.65) * mm});
            skLineSegment(sketch, "E679", {"start": v(-61.17, -82.65) * mm, "end": v(-60.88, -82.92) * mm});
            skLineSegment(sketch, "E680", {"start": v(-60.88, -82.92) * mm, "end": v(-60.3, -83.04) * mm});
            skLineSegment(sketch, "E681", {"start": v(-60.3, -83.04) * mm, "end": v(-59.74, -83.17) * mm});
            skLineSegment(sketch, "E682", {"start": v(-59.74, -83.17) * mm, "end": v(-59.17, -83.3) * mm});
            skLineSegment(sketch, "E683", {"start": v(-59.17, -83.3) * mm, "end": v(-58.6, -83.42) * mm});
            skLineSegment(sketch, "E684", {"start": v(-58.6, -83.42) * mm, "end": v(-58.03, -83.54) * mm});
            skLineSegment(sketch, "E685", {"start": v(-58.03, -83.54) * mm, "end": v(-57.46, -83.67) * mm});
            skLineSegment(sketch, "E686", {"start": v(-57.46, -83.67) * mm, "end": v(-56.89, -83.79) * mm});
            skLineSegment(sketch, "E687", {"start": v(-56.89, -83.79) * mm, "end": v(-56.32, -83.91) * mm});
            skLineSegment(sketch, "E688", {"start": v(-56.32, -83.91) * mm, "end": v(-55.75, -84.04) * mm});
            skLineSegment(sketch, "E689", {"start": v(-55.75, -84.04) * mm, "end": v(-55.18, -84.16) * mm});
            skLineSegment(sketch, "E690", {"start": v(-55.18, -84.16) * mm, "end": v(-54.6, -84.29) * mm});
            skLineSegment(sketch, "E691", {"start": v(-54.6, -84.29) * mm, "end": v(-54.03, -84.41) * mm});
            skLineSegment(sketch, "E692", {"start": v(-54.03, -84.41) * mm, "end": v(-53.46, -84.54) * mm});
            skLineSegment(sketch, "E693", {"start": v(-53.46, -84.54) * mm, "end": v(-52.9, -84.66) * mm});
            skLineSegment(sketch, "E694", {"start": v(-52.9, -84.66) * mm, "end": v(-52.32, -84.79) * mm});
            skLineSegment(sketch, "E695", {"start": v(-52.32, -84.79) * mm, "end": v(-51.75, -84.91) * mm});
            skLineSegment(sketch, "E696", {"start": v(-51.75, -84.91) * mm, "end": v(-51.18, -85.04) * mm});
            skLineSegment(sketch, "E697", {"start": v(-51.18, -85.04) * mm, "end": v(-50.61, -85.16) * mm});
            skLineSegment(sketch, "E698", {"start": v(-50.61, -85.16) * mm, "end": v(-50.04, -85.29) * mm});
            skLineSegment(sketch, "E699", {"start": v(-50.04, -85.29) * mm, "end": v(-49.84, -85.28) * mm});
            skLineSegment(sketch, "E700", {"start": v(-49.84, -85.28) * mm, "end": v(-49.67, -85.17) * mm});
            skLineSegment(sketch, "E701", {"start": v(-49.67, -85.17) * mm, "end": v(-49.27, -84.74) * mm});
            skLineSegment(sketch, "E702", {"start": v(-49.27, -84.74) * mm, "end": v(-48.88, -84.3) * mm});
            skLineSegment(sketch, "E703", {"start": v(-48.88, -84.3) * mm, "end": v(-48.49, -83.87) * mm});
            skLineSegment(sketch, "E704", {"start": v(-48.49, -83.87) * mm, "end": v(-48.1, -83.44) * mm});
            skLineSegment(sketch, "E705", {"start": v(-48.1, -83.44) * mm, "end": v(-47.7, -83.01) * mm});
            skLineSegment(sketch, "E706", {"start": v(-47.7, -83.01) * mm, "end": v(-47.3, -82.58) * mm});
            skLineSegment(sketch, "E707", {"start": v(-47.3, -82.58) * mm, "end": v(-46.91, -82.15) * mm});
            skLineSegment(sketch, "E708", {"start": v(-46.91, -82.15) * mm, "end": v(-46.52, -81.72) * mm});
            skLineSegment(sketch, "E709", {"start": v(-46.52, -81.72) * mm, "end": v(-46.13, -81.29) * mm});
            skLineSegment(sketch, "E710", {"start": v(-46.13, -81.29) * mm, "end": v(-45.73, -80.85) * mm});
            skLineSegment(sketch, "E711", {"start": v(-45.73, -80.85) * mm, "end": v(-45.34, -80.42) * mm});
            skLineSegment(sketch, "E712", {"start": v(-45.34, -80.42) * mm, "end": v(-44.95, -80) * mm});
            skLineSegment(sketch, "E713", {"start": v(-44.95, -80) * mm, "end": v(-44.55, -79.56) * mm});
            skLineSegment(sketch, "E714", {"start": v(-44.55, -79.56) * mm, "end": v(-44.16, -79.13) * mm});
            skLineSegment(sketch, "E715", {"start": v(-44.16, -79.13) * mm, "end": v(-43.77, -78.7) * mm});
            skLineSegment(sketch, "E716", {"start": v(-43.77, -78.7) * mm, "end": v(-43.37, -78.27) * mm});
            skLineSegment(sketch, "E717", {"start": v(-43.37, -78.27) * mm, "end": v(-42.98, -77.83) * mm});
            skLineSegment(sketch, "E718", {"start": v(-42.98, -77.83) * mm, "end": v(-42.59, -77.4) * mm});
            skLineSegment(sketch, "E719", {"start": v(-42.59, -77.4) * mm, "end": v(-42.2, -76.97) * mm});
            skLineSegment(sketch, "E720", {"start": v(-42.2, -76.97) * mm, "end": v(-42.1, -76.59) * mm});
            skLineSegment(sketch, "E721", {"start": v(-42.1, -76.59) * mm, "end": v(-42.29, -76.03) * mm});
            skLineSegment(sketch, "E722", {"start": v(-42.29, -76.03) * mm, "end": v(-42.46, -75.47) * mm});
            skLineSegment(sketch, "E723", {"start": v(-42.46, -75.47) * mm, "end": v(-42.64, -74.92) * mm});
            skLineSegment(sketch, "E724", {"start": v(-42.64, -74.92) * mm, "end": v(-42.82, -74.36) * mm});
            skLineSegment(sketch, "E725", {"start": v(-42.82, -74.36) * mm, "end": v(-43, -73.8) * mm});
            skLineSegment(sketch, "E726", {"start": v(-43, -73.8) * mm, "end": v(-43.17, -73.25) * mm});
            skLineSegment(sketch, "E727", {"start": v(-43.17, -73.25) * mm, "end": v(-43.35, -72.7) * mm});
            skLineSegment(sketch, "E728", {"start": v(-43.35, -72.7) * mm, "end": v(-43.52, -72.14) * mm});
            skLineSegment(sketch, "E729", {"start": v(-43.52, -72.14) * mm, "end": v(-43.7, -71.58) * mm});
            skLineSegment(sketch, "E730", {"start": v(-43.7, -71.58) * mm, "end": v(-43.88, -71.02) * mm});
            skLineSegment(sketch, "E731", {"start": v(-43.88, -71.02) * mm, "end": v(-44.06, -70.47) * mm});
            skLineSegment(sketch, "E732", {"start": v(-44.06, -70.47) * mm, "end": v(-44.23, -69.91) * mm});
            skLineSegment(sketch, "E733", {"start": v(-44.23, -69.91) * mm, "end": v(-44.4, -69.36) * mm});
            skLineSegment(sketch, "E734", {"start": v(-44.4, -69.36) * mm, "end": v(-44.59, -68.8) * mm});
            skLineSegment(sketch, "E735", {"start": v(-44.59, -68.8) * mm, "end": v(-44.76, -68.24) * mm});
            skLineSegment(sketch, "E736", {"start": v(-44.76, -68.24) * mm, "end": v(-44.94, -67.69) * mm});
            skLineSegment(sketch, "E737", {"start": v(-44.94, -67.69) * mm, "end": v(-45.12, -67.13) * mm});
            skLineSegment(sketch, "E738", {"start": v(-45.12, -67.13) * mm, "end": v(-45.3, -66.57) * mm});
            skLineSegment(sketch, "E739", {"start": v(-45.3, -66.57) * mm, "end": v(-45.47, -66.02) * mm});
            skLineSegment(sketch, "E740", {"start": v(-45.47, -66.02) * mm, "end": v(-45.76, -65.75) * mm});
            skLineSegment(sketch, "E741", {"start": v(-51.89, -71.77) * mm, "end": v(-51.4, -71.61) * mm});
            skLineSegment(sketch, "E742", {"start": v(-51.4, -71.61) * mm, "end": v(-50.91, -71.46) * mm});
            skLineSegment(sketch, "E743", {"start": v(-50.91, -71.46) * mm, "end": v(-50.43, -71.3) * mm});
            skLineSegment(sketch, "E744", {"start": v(-50.43, -71.3) * mm, "end": v(-49.94, -71.15) * mm});
            skLineSegment(sketch, "E745", {"start": v(-49.94, -71.15) * mm, "end": v(-49.77, -71.56) * mm});
            skLineSegment(sketch, "E746", {"start": v(-49.77, -71.56) * mm, "end": v(-49.6, -71.96) * mm});
            skLineSegment(sketch, "E747", {"start": v(-49.6, -71.96) * mm, "end": v(-49.4, -71.54) * mm});
            skLineSegment(sketch, "E748", {"start": v(-49.4, -71.54) * mm, "end": v(-49.11, -71.09) * mm});
            skLineSegment(sketch, "E749", {"start": v(-49.11, -71.09) * mm, "end": v(-48.84, -70.81) * mm});
            skLineSegment(sketch, "E750", {"start": v(-48.84, -70.81) * mm, "end": v(-48.49, -70.59) * mm});
            skLineSegment(sketch, "E751", {"start": v(-48.49, -70.59) * mm, "end": v(-48.06, -70.41) * mm});
            skLineSegment(sketch, "E752", {"start": v(-48.06, -70.41) * mm, "end": v(-47.59, -70.3) * mm});
            skLineSegment(sketch, "E753", {"start": v(-47.59, -70.3) * mm, "end": v(-47.18, -70.27) * mm});
            skLineSegment(sketch, "E754", {"start": v(-47.18, -70.27) * mm, "end": v(-47.12, -70.75) * mm});
            skLineSegment(sketch, "E755", {"start": v(-47.12, -70.75) * mm, "end": v(-47.06, -71.22) * mm});
            skLineSegment(sketch, "E756", {"start": v(-47.06, -71.22) * mm, "end": v(-47, -71.7) * mm});
            skLineSegment(sketch, "E757", {"start": v(-47, -71.7) * mm, "end": v(-46.93, -72.17) * mm});
            skLineSegment(sketch, "E758", {"start": v(-46.93, -72.17) * mm, "end": v(-47.3, -72.2) * mm});
            skLineSegment(sketch, "E759", {"start": v(-47.3, -72.2) * mm, "end": v(-47.7, -72.3) * mm});
            skLineSegment(sketch, "E760", {"start": v(-47.7, -72.3) * mm, "end": v(-48.13, -72.5) * mm});
            skLineSegment(sketch, "E761", {"start": v(-48.13, -72.5) * mm, "end": v(-48.48, -72.76) * mm});
            skLineSegment(sketch, "E762", {"start": v(-48.48, -72.76) * mm, "end": v(-48.73, -73.1) * mm});
            skLineSegment(sketch, "E763", {"start": v(-48.73, -73.1) * mm, "end": v(-48.87, -73.51) * mm});
            skLineSegment(sketch, "E764", {"start": v(-48.87, -73.51) * mm, "end": v(-48.89, -73.97) * mm});
            skLineSegment(sketch, "E765", {"start": v(-48.89, -73.97) * mm, "end": v(-48.78, -74.47) * mm});
            skLineSegment(sketch, "E766", {"start": v(-48.78, -74.47) * mm, "end": v(-48.6, -75.02) * mm});
            skLineSegment(sketch, "E767", {"start": v(-48.6, -75.02) * mm, "end": v(-48.44, -75.57) * mm});
            skLineSegment(sketch, "E768", {"start": v(-48.44, -75.57) * mm, "end": v(-48.26, -76.11) * mm});
            skLineSegment(sketch, "E769", {"start": v(-48.26, -76.11) * mm, "end": v(-48.09, -76.66) * mm});
            skLineSegment(sketch, "E770", {"start": v(-48.09, -76.66) * mm, "end": v(-47.91, -77.2) * mm});
            skLineSegment(sketch, "E771", {"start": v(-47.91, -77.2) * mm, "end": v(-47.74, -77.75) * mm});
            skLineSegment(sketch, "E772", {"start": v(-47.74, -77.75) * mm, "end": v(-48.25, -77.91) * mm});
            skLineSegment(sketch, "E773", {"start": v(-48.25, -77.91) * mm, "end": v(-48.76, -78.08) * mm});
            skLineSegment(sketch, "E774", {"start": v(-48.76, -78.08) * mm, "end": v(-49.27, -78.24) * mm});
            skLineSegment(sketch, "E775", {"start": v(-49.27, -78.24) * mm, "end": v(-49.78, -78.4) * mm});
            skLineSegment(sketch, "E776", {"start": v(-49.78, -78.4) * mm, "end": v(-49.95, -77.85) * mm});
            skLineSegment(sketch, "E777", {"start": v(-49.95, -77.85) * mm, "end": v(-50.13, -77.3) * mm});
            skLineSegment(sketch, "E778", {"start": v(-50.13, -77.3) * mm, "end": v(-50.3, -76.74) * mm});
            skLineSegment(sketch, "E779", {"start": v(-50.3, -76.74) * mm, "end": v(-50.48, -76.2) * mm});
            skLineSegment(sketch, "E780", {"start": v(-50.48, -76.2) * mm, "end": v(-50.65, -75.64) * mm});
            skLineSegment(sketch, "E781", {"start": v(-50.65, -75.64) * mm, "end": v(-50.83, -75.08) * mm});
            skLineSegment(sketch, "E782", {"start": v(-50.83, -75.08) * mm, "end": v(-51, -74.53) * mm});
            skLineSegment(sketch, "E783", {"start": v(-51, -74.53) * mm, "end": v(-51.18, -73.98) * mm});
            skLineSegment(sketch, "E784", {"start": v(-51.18, -73.98) * mm, "end": v(-51.36, -73.43) * mm});
            skLineSegment(sketch, "E785", {"start": v(-51.36, -73.43) * mm, "end": v(-51.53, -72.87) * mm});
            skLineSegment(sketch, "E786", {"start": v(-51.53, -72.87) * mm, "end": v(-51.7, -72.32) * mm});
            skLineSegment(sketch, "E787", {"start": v(-51.7, -72.32) * mm, "end": v(-51.89, -71.77) * mm});
            skLineSegment(sketch, "E788", {"start": v(-51.89, -71.77) * mm, "end": v(-51.89, -71.77) * mm});
            skLineSegment(sketch, "E789", {"start": v(-60.78, -71.51) * mm, "end": v(-60.28, -71.35) * mm});
            skLineSegment(sketch, "E790", {"start": v(-60.28, -71.35) * mm, "end": v(-59.77, -71.2) * mm});
            skLineSegment(sketch, "E791", {"start": v(-59.77, -71.2) * mm, "end": v(-59.27, -71.03) * mm});
            skLineSegment(sketch, "E792", {"start": v(-59.27, -71.03) * mm, "end": v(-58.76, -70.87) * mm});
            skLineSegment(sketch, "E793", {"start": v(-58.76, -70.87) * mm, "end": v(-58.26, -70.71) * mm});
            skLineSegment(sketch, "E794", {"start": v(-58.26, -70.71) * mm, "end": v(-57.75, -70.55) * mm});
            skLineSegment(sketch, "E795", {"start": v(-57.75, -70.55) * mm, "end": v(-57.25, -70.39) * mm});
            skLineSegment(sketch, "E796", {"start": v(-57.25, -70.39) * mm, "end": v(-56.68, -70.24) * mm});
            skLineSegment(sketch, "E797", {"start": v(-56.68, -70.24) * mm, "end": v(-56.17, -70.15) * mm});
            skLineSegment(sketch, "E798", {"start": v(-56.17, -70.15) * mm, "end": v(-55.7, -70.12) * mm});
            skLineSegment(sketch, "E799", {"start": v(-55.7, -70.12) * mm, "end": v(-55.27, -70.15) * mm});
            skLineSegment(sketch, "E800", {"start": v(-55.27, -70.15) * mm, "end": v(-54.88, -70.23) * mm});
            skLineSegment(sketch, "E801", {"start": v(-54.88, -70.23) * mm, "end": v(-54.53, -70.35) * mm});
            skLineSegment(sketch, "E802", {"start": v(-54.53, -70.35) * mm, "end": v(-54.09, -70.61) * mm});
            skLineSegment(sketch, "E803", {"start": v(-54.09, -70.61) * mm, "end": v(-53.73, -70.96) * mm});
            skLineSegment(sketch, "E804", {"start": v(-53.73, -70.96) * mm, "end": v(-53.46, -71.37) * mm});
            skLineSegment(sketch, "E805", {"start": v(-53.46, -71.37) * mm, "end": v(-53.27, -71.83) * mm});
            skLineSegment(sketch, "E806", {"start": v(-53.27, -71.83) * mm, "end": v(-53.17, -72.27) * mm});
            skLineSegment(sketch, "E807", {"start": v(-53.17, -72.27) * mm, "end": v(-53.18, -72.68) * mm});
            skLineSegment(sketch, "E808", {"start": v(-53.18, -72.68) * mm, "end": v(-53.25, -73.06) * mm});
            skLineSegment(sketch, "E809", {"start": v(-53.25, -73.06) * mm, "end": v(-53.37, -73.4) * mm});
            skLineSegment(sketch, "E810", {"start": v(-53.37, -73.4) * mm, "end": v(-53.52, -73.7) * mm});
            skLineSegment(sketch, "E811", {"start": v(-53.52, -73.7) * mm, "end": v(-53.71, -73.93) * mm});
            skLineSegment(sketch, "E812", {"start": v(-53.71, -73.93) * mm, "end": v(-54.06, -74.25) * mm});
            skLineSegment(sketch, "E813", {"start": v(-54.06, -74.25) * mm, "end": v(-53.77, -74.25) * mm});
            skLineSegment(sketch, "E814", {"start": v(-53.77, -74.25) * mm, "end": v(-53.42, -74.28) * mm});
            skLineSegment(sketch, "E815", {"start": v(-53.42, -74.28) * mm, "end": v(-53.04, -74.35) * mm});
            skLineSegment(sketch, "E816", {"start": v(-53.04, -74.35) * mm, "end": v(-52.66, -74.5) * mm});
            skLineSegment(sketch, "E817", {"start": v(-52.66, -74.5) * mm, "end": v(-52.28, -74.72) * mm});
            skLineSegment(sketch, "E818", {"start": v(-52.28, -74.72) * mm, "end": v(-51.93, -75.03) * mm});
            skLineSegment(sketch, "E819", {"start": v(-51.93, -75.03) * mm, "end": v(-51.63, -75.43) * mm});
            skLineSegment(sketch, "E820", {"start": v(-51.63, -75.43) * mm, "end": v(-51.41, -75.94) * mm});
            skLineSegment(sketch, "E821", {"start": v(-51.41, -75.94) * mm, "end": v(-51.3, -76.42) * mm});
            skLineSegment(sketch, "E822", {"start": v(-51.3, -76.42) * mm, "end": v(-51.25, -76.86) * mm});
            skLineSegment(sketch, "E823", {"start": v(-51.25, -76.86) * mm, "end": v(-51.28, -77.27) * mm});
            skLineSegment(sketch, "E824", {"start": v(-51.28, -77.27) * mm, "end": v(-51.45, -77.83) * mm});
            skLineSegment(sketch, "E825", {"start": v(-51.45, -77.83) * mm, "end": v(-51.75, -78.34) * mm});
            skLineSegment(sketch, "E826", {"start": v(-51.75, -78.34) * mm, "end": v(-52.02, -78.64) * mm});
            skLineSegment(sketch, "E827", {"start": v(-52.02, -78.64) * mm, "end": v(-52.36, -78.92) * mm});
            skLineSegment(sketch, "E828", {"start": v(-52.36, -78.92) * mm, "end": v(-52.76, -79.18) * mm});
            skLineSegment(sketch, "E829", {"start": v(-52.76, -79.18) * mm, "end": v(-53.2, -79.41) * mm});
            skLineSegment(sketch, "E830", {"start": v(-53.2, -79.41) * mm, "end": v(-53.7, -79.63) * mm});
            skLineSegment(sketch, "E831", {"start": v(-53.7, -79.63) * mm, "end": v(-54.24, -79.82) * mm});
            skLineSegment(sketch, "E832", {"start": v(-54.24, -79.82) * mm, "end": v(-54.75, -79.98) * mm});
            skLineSegment(sketch, "E833", {"start": v(-54.75, -79.98) * mm, "end": v(-55.25, -80.14) * mm});
            skLineSegment(sketch, "E834", {"start": v(-55.25, -80.14) * mm, "end": v(-55.76, -80.3) * mm});
            skLineSegment(sketch, "E835", {"start": v(-55.76, -80.3) * mm, "end": v(-56.26, -80.46) * mm});
            skLineSegment(sketch, "E836", {"start": v(-56.26, -80.46) * mm, "end": v(-56.77, -80.62) * mm});
            skLineSegment(sketch, "E837", {"start": v(-56.77, -80.62) * mm, "end": v(-57.27, -80.78) * mm});
            skLineSegment(sketch, "E838", {"start": v(-57.27, -80.78) * mm, "end": v(-57.78, -80.94) * mm});
            skLineSegment(sketch, "E839", {"start": v(-57.78, -80.94) * mm, "end": v(-57.96, -80.39) * mm});
            skLineSegment(sketch, "E840", {"start": v(-57.96, -80.39) * mm, "end": v(-58.13, -79.83) * mm});
            skLineSegment(sketch, "E841", {"start": v(-58.13, -79.83) * mm, "end": v(-58.3, -79.28) * mm});
            skLineSegment(sketch, "E842", {"start": v(-58.3, -79.28) * mm, "end": v(-58.49, -78.73) * mm});
            skLineSegment(sketch, "E843", {"start": v(-58.49, -78.73) * mm, "end": v(-58.66, -78.17) * mm});
            skLineSegment(sketch, "E844", {"start": v(-58.66, -78.17) * mm, "end": v(-58.84, -77.62) * mm});
            skLineSegment(sketch, "E845", {"start": v(-58.84, -77.62) * mm, "end": v(-59.02, -77.06) * mm});
            skLineSegment(sketch, "E846", {"start": v(-59.02, -77.06) * mm, "end": v(-59.2, -76.5) * mm});
            skLineSegment(sketch, "E847", {"start": v(-59.2, -76.5) * mm, "end": v(-59.37, -75.95) * mm});
            skLineSegment(sketch, "E848", {"start": v(-59.37, -75.95) * mm, "end": v(-59.54, -75.4) * mm});
            skLineSegment(sketch, "E849", {"start": v(-59.54, -75.4) * mm, "end": v(-59.72, -74.84) * mm});
            skLineSegment(sketch, "E850", {"start": v(-59.72, -74.84) * mm, "end": v(-59.9, -74.29) * mm});
            skLineSegment(sketch, "E851", {"start": v(-59.9, -74.29) * mm, "end": v(-60.07, -73.73) * mm});
            skLineSegment(sketch, "E852", {"start": v(-60.07, -73.73) * mm, "end": v(-60.25, -73.18) * mm});
            skLineSegment(sketch, "E853", {"start": v(-60.25, -73.18) * mm, "end": v(-60.43, -72.62) * mm});
            skLineSegment(sketch, "E854", {"start": v(-60.43, -72.62) * mm, "end": v(-60.6, -72.07) * mm});
            skLineSegment(sketch, "E855", {"start": v(-60.6, -72.07) * mm, "end": v(-60.78, -71.51) * mm});
            skLineSegment(sketch, "E856", {"start": v(-54.84, -78.2) * mm, "end": v(-54.34, -78) * mm});
            skLineSegment(sketch, "E857", {"start": v(-54.34, -78) * mm, "end": v(-53.87, -77.68) * mm});
            skLineSegment(sketch, "E858", {"start": v(-53.87, -77.68) * mm, "end": v(-53.58, -77.18) * mm});
            skLineSegment(sketch, "E859", {"start": v(-53.58, -77.18) * mm, "end": v(-53.55, -76.86) * mm});
            skLineSegment(sketch, "E860", {"start": v(-53.55, -76.86) * mm, "end": v(-53.63, -76.47) * mm});
            skLineSegment(sketch, "E861", {"start": v(-53.63, -76.47) * mm, "end": v(-53.78, -76.13) * mm});
            skLineSegment(sketch, "E862", {"start": v(-53.78, -76.13) * mm, "end": v(-53.99, -75.9) * mm});
            skLineSegment(sketch, "E863", {"start": v(-53.99, -75.9) * mm, "end": v(-54.5, -75.64) * mm});
            skLineSegment(sketch, "E864", {"start": v(-54.5, -75.64) * mm, "end": v(-55.09, -75.63) * mm});
            skLineSegment(sketch, "E865", {"start": v(-55.09, -75.63) * mm, "end": v(-55.63, -75.74) * mm});
            skLineSegment(sketch, "E866", {"start": v(-55.63, -75.74) * mm, "end": v(-56.09, -75.89) * mm});
            skLineSegment(sketch, "E867", {"start": v(-56.09, -75.89) * mm, "end": v(-56.55, -76.04) * mm});
            skLineSegment(sketch, "E868", {"start": v(-56.55, -76.04) * mm, "end": v(-57.01, -76.18) * mm});
            skLineSegment(sketch, "E869", {"start": v(-57.01, -76.18) * mm, "end": v(-56.85, -76.68) * mm});
            skLineSegment(sketch, "E870", {"start": v(-56.85, -76.68) * mm, "end": v(-56.7, -77.17) * mm});
            skLineSegment(sketch, "E871", {"start": v(-56.7, -77.17) * mm, "end": v(-56.54, -77.66) * mm});
            skLineSegment(sketch, "E872", {"start": v(-56.54, -77.66) * mm, "end": v(-56.38, -78.15) * mm});
            skLineSegment(sketch, "E873", {"start": v(-56.38, -78.15) * mm, "end": v(-56.23, -78.65) * mm});
            skLineSegment(sketch, "E874", {"start": v(-56.23, -78.65) * mm, "end": v(-55.76, -78.5) * mm});
            skLineSegment(sketch, "E875", {"start": v(-55.76, -78.5) * mm, "end": v(-55.3, -78.35) * mm});
            skLineSegment(sketch, "E876", {"start": v(-55.3, -78.35) * mm, "end": v(-54.84, -78.2) * mm});
            skLineSegment(sketch, "E877", {"start": v(-56.24, -74.23) * mm, "end": v(-55.79, -74.02) * mm});
            skLineSegment(sketch, "E878", {"start": v(-55.79, -74.02) * mm, "end": v(-55.44, -73.71) * mm});
            skLineSegment(sketch, "E879", {"start": v(-55.44, -73.71) * mm, "end": v(-55.25, -73.3) * mm});
            skLineSegment(sketch, "E880", {"start": v(-55.25, -73.3) * mm, "end": v(-55.3, -72.76) * mm});
            skLineSegment(sketch, "E881", {"start": v(-55.3, -72.76) * mm, "end": v(-55.57, -72.28) * mm});
            skLineSegment(sketch, "E882", {"start": v(-55.57, -72.28) * mm, "end": v(-55.97, -72.05) * mm});
            skLineSegment(sketch, "E883", {"start": v(-55.97, -72.05) * mm, "end": v(-56.44, -72.02) * mm});
            skLineSegment(sketch, "E884", {"start": v(-56.44, -72.02) * mm, "end": v(-56.92, -72.11) * mm});
            skLineSegment(sketch, "E885", {"start": v(-56.92, -72.11) * mm, "end": v(-57.34, -72.24) * mm});
            skLineSegment(sketch, "E886", {"start": v(-57.34, -72.24) * mm, "end": v(-57.76, -72.38) * mm});
            skLineSegment(sketch, "E887", {"start": v(-57.76, -72.38) * mm, "end": v(-58.18, -72.51) * mm});
            skLineSegment(sketch, "E888", {"start": v(-58.18, -72.51) * mm, "end": v(-58, -73.04) * mm});
            skLineSegment(sketch, "E889", {"start": v(-58, -73.04) * mm, "end": v(-57.84, -73.57) * mm});
            skLineSegment(sketch, "E890", {"start": v(-57.84, -73.57) * mm, "end": v(-57.67, -74.1) * mm});
            skLineSegment(sketch, "E891", {"start": v(-57.67, -74.1) * mm, "end": v(-57.5, -74.63) * mm});
            skLineSegment(sketch, "E892", {"start": v(-57.5, -74.63) * mm, "end": v(-57.08, -74.5) * mm});
            skLineSegment(sketch, "E893", {"start": v(-57.08, -74.5) * mm, "end": v(-56.66, -74.37) * mm});
            skLineSegment(sketch, "E894", {"start": v(-56.66, -74.37) * mm, "end": v(-56.24, -74.23) * mm});
            skLineSegment(sketch, "E895", {"start": v(-56.24, -74.23) * mm, "end": v(-56.24, -74.23) * mm});
            skLineSegment(sketch, "E896", {"start": v(14.25, 22.95) * mm, "end": v(29.25, 22.95) * mm});
            skLineSegment(sketch, "E897", {"start": v(29.25, 22.95) * mm, "end": v(29.25, 25.95) * mm});
            skLineSegment(sketch, "E898", {"start": v(29.25, 25.95) * mm, "end": v(14.25, 25.95) * mm});
            skLineSegment(sketch, "E899", {"start": v(14.25, 25.95) * mm, "end": v(14.25, 22.95) * mm});
            skLineSegment(sketch, "E900", {"start": v(44.25, 70.46) * mm, "end": v(59.25, 70.46) * mm});
            skLineSegment(sketch, "E901", {"start": v(59.25, 70.46) * mm, "end": v(59.25, 73.45) * mm});
            skLineSegment(sketch, "E902", {"start": v(59.25, 73.45) * mm, "end": v(44.25, 73.45) * mm});
            skLineSegment(sketch, "E903", {"start": v(44.25, 73.45) * mm, "end": v(44.25, 70.46) * mm});
            skLineSegment(sketch, "E904", {"start": v(14.25, 70.45) * mm, "end": v(29.25, 70.45) * mm});
            skLineSegment(sketch, "E905", {"start": v(29.25, 70.45) * mm, "end": v(29.25, 73.45) * mm});
            skLineSegment(sketch, "E906", {"start": v(29.25, 73.45) * mm, "end": v(14.25, 73.45) * mm});
            skLineSegment(sketch, "E907", {"start": v(14.25, 73.45) * mm, "end": v(14.25, 70.45) * mm});
            skLineSegment(sketch, "E908", {"start": v(44.25, 22.95) * mm, "end": v(59.25, 22.95) * mm});
            skLineSegment(sketch, "E909", {"start": v(59.25, 22.95) * mm, "end": v(59.25, 25.95) * mm});
            skLineSegment(sketch, "E910", {"start": v(59.25, 25.95) * mm, "end": v(44.25, 25.95) * mm});
            skLineSegment(sketch, "E911", {"start": v(44.25, 25.95) * mm, "end": v(44.25, 22.95) * mm});
            skSolve(sketch);
        }
        {
            var Q0;
            Q0=makeQuery(id+"F0.imprint","IMPRINT",FACE,{"disambiguationData":[TD([[makeQuery(id+"F0.imprint","IMPRINT",EDGE,{"derivedFrom":sQuery(id+"F0.wireOp",EDGE,"E50")}),-1.0]])]});
            var Q1;
            {var subQ0=sQuery(id+"F0.wireOp",EDGE,"E7");Q1=makeQuery(id+"F0.imprint","IMPRINT",FACE,{"disambiguationData":[TD([[makeQuery(id+"F0.imprint","IMPRINT",EDGE,{"derivedFrom":subQ0}),-1.0]])]});}
            var Q2;
            Q2=makeQuery(id+"F0.imprint","IMPRINT",FACE,{"disambiguationData":[TD([[makeQuery(id+"F0.imprint","IMPRINT",EDGE,{"derivedFrom":sQuery(id+"F0.wireOp",EDGE,"E0")}),1.0]])]});
            var Q3;
            Q3=makeQuery(id+"F0.imprint","IMPRINT",FACE,{"disambiguationData":[TD([[makeQuery(id+"F0.imprint","IMPRINT",EDGE,{"derivedFrom":sQuery(id+"F0.wireOp",EDGE,"E256")}),-1.0]])]});
            var Q4;
            Q4=makeQuery(id+"F0.imprint","IMPRINT",FACE,{"disambiguationData":[TD([[makeQuery(id+"F0.imprint","IMPRINT",EDGE,{"derivedFrom":sQuery(id+"F0.wireOp",EDGE,"E208")}),-1.0]])]});
            var Q5;
            Q5=makeQuery(id+"F0.imprint","IMPRINT",FACE,{"disambiguationData":[TD([[makeQuery(id+"F0.imprint","IMPRINT",EDGE,{"derivedFrom":sQuery(id+"F0.wireOp",EDGE,"E513")}),-1.0]])]});
            var Q6;
            Q6=makeQuery(id+"F0.imprint","IMPRINT",FACE,{"disambiguationData":[TD([[makeQuery(id+"F0.imprint","IMPRINT",EDGE,{"derivedFrom":sQuery(id+"F0.wireOp",EDGE,"E465")}),-1.0]])]});
            var Q7;
            Q7=makeQuery(id+"F0.imprint","IMPRINT",FACE,{"disambiguationData":[TD([[makeQuery(id+"F0.imprint","IMPRINT",EDGE,{"derivedFrom":sQuery(id+"F0.wireOp",EDGE,"E741")}),-1.0]])]});
            var Q8;
            Q8=makeQuery(id+"F0.imprint","IMPRINT",FACE,{"disambiguationData":[TD([[makeQuery(id+"F0.imprint","IMPRINT",EDGE,{"derivedFrom":sQuery(id+"F0.wireOp",EDGE,"E789")}),-1.0]])]});
            extrude(context, id + "F1", {"entities" : qUnion([Q0, Q1, Q2, Q3, Q4, Q5, Q6, Q7, Q8]), "depth" : 3 * mm});
        }
        {
            var Q0;
            Q0=makeQuery(id+"F0.imprint","IMPRINT",FACE,{"disambiguationData":[TD([[makeQuery(id+"F0.imprint","IMPRINT",EDGE,{"derivedFrom":sQuery(id+"F0.wireOp",EDGE,"E620")}),1.0]])]});
            var Q1;
            Q1=makeQuery(id+"F0.imprint","IMPRINT",FACE,{"disambiguationData":[TD([[makeQuery(id+"F0.imprint","IMPRINT",EDGE,{"derivedFrom":sQuery(id+"F0.wireOp",EDGE,"E877")}),1.0]])]});
            var Q2;
            Q2=makeQuery(id+"F0.imprint","IMPRINT",FACE,{"disambiguationData":[TD([[makeQuery(id+"F0.imprint","IMPRINT",EDGE,{"derivedFrom":sQuery(id+"F0.wireOp",EDGE,"E856")}),1.0]])]});
            var Q3;
            Q3=makeQuery(id+"F0.imprint","IMPRINT",FACE,{"disambiguationData":[TD([[makeQuery(id+"F0.imprint","IMPRINT",EDGE,{"derivedFrom":sQuery(id+"F0.wireOp",EDGE,"E344")}),1.0]])]});
            var Q4;
            Q4=makeQuery(id+"F0.imprint","IMPRINT",FACE,{"disambiguationData":[TD([[makeQuery(id+"F0.imprint","IMPRINT",EDGE,{"derivedFrom":sQuery(id+"F0.wireOp",EDGE,"E601")}),1.0]])]});
            var Q5;
            Q5=makeQuery(id+"F0.imprint","IMPRINT",FACE,{"disambiguationData":[TD([[makeQuery(id+"F0.imprint","IMPRINT",EDGE,{"derivedFrom":sQuery(id+"F0.wireOp",EDGE,"E580")}),1.0]])]});
            var Q6;
            Q6=makeQuery(id+"F0.imprint","IMPRINT",FACE,{"disambiguationData":[TD([[makeQuery(id+"F0.imprint","IMPRINT",EDGE,{"derivedFrom":sQuery(id+"F0.wireOp",EDGE,"E68")}),1.0]])]});
            var Q7;
            Q7=makeQuery(id+"F0.imprint","IMPRINT",FACE,{"disambiguationData":[TD([[makeQuery(id+"F0.imprint","IMPRINT",EDGE,{"derivedFrom":sQuery(id+"F0.wireOp",EDGE,"E189")}),1.0]])]});
            var Q8;
            Q8=makeQuery(id+"F0.imprint","IMPRINT",FACE,{"disambiguationData":[TD([[makeQuery(id+"F0.imprint","IMPRINT",EDGE,{"derivedFrom":sQuery(id+"F0.wireOp",EDGE,"E323")}),1.0]])]});
            extrude(context, id + "F2", {"entities" : qUnion([Q0, Q1, Q2, Q3, Q4, Q5, Q6, Q7, Q8]), "operationType" : NewBodyOperationType.ADD, "depth" : 2 * mm});
        }
    });
